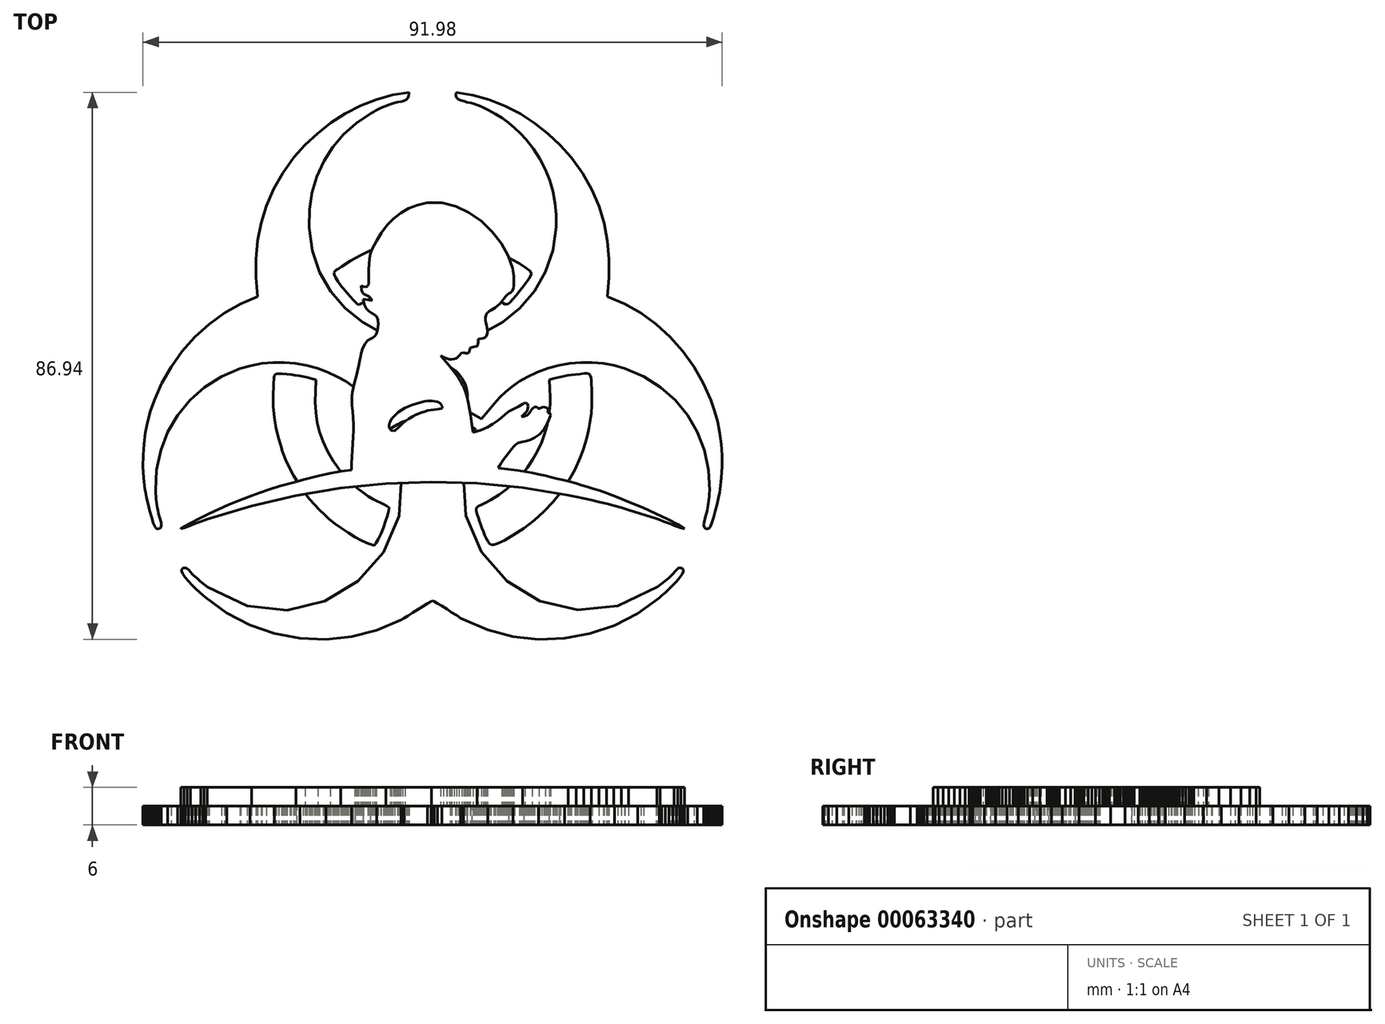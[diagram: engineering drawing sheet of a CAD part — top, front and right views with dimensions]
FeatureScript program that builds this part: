
annotation { "Feature Type Name" : "Feature", "Feature Type Description" : "" }
export const myFeature = defineFeature(function(context is Context, id is Id, definition is map)
    precondition{}
    {
        {
            var Q0;
            Q0=qCreatedBy(makeId("Top.planeOp"),FACE);
            var sketch = newSketch(context, id + "F0", { "sketchPlane" : qUnion([Q0])});
            skLineSegment(sketch, "E0", {"start": v(-39.96, -25.84) * mm, "end": v(-40, -25.92) * mm});
            skLineSegment(sketch, "E1", {"start": v(-40, -25.92) * mm, "end": v(-39.49, -25.75) * mm});
            skLineSegment(sketch, "E2", {"start": v(-39.49, -25.75) * mm, "end": v(-38.96, -25.56) * mm});
            skLineSegment(sketch, "E3", {"start": v(-38.96, -25.56) * mm, "end": v(-38.44, -25.37) * mm});
            skLineSegment(sketch, "E4", {"start": v(-38.44, -25.37) * mm, "end": v(-37.9, -25.16) * mm});
            skLineSegment(sketch, "E5", {"start": v(-37.9, -25.16) * mm, "end": v(-37.38, -24.95) * mm});
            skLineSegment(sketch, "E6", {"start": v(-37.38, -24.95) * mm, "end": v(-36.84, -24.75) * mm});
            skLineSegment(sketch, "E7", {"start": v(-36.84, -24.75) * mm, "end": v(-36.3, -24.55) * mm});
            skLineSegment(sketch, "E8", {"start": v(-36.3, -24.55) * mm, "end": v(-35.77, -24.36) * mm});
            skLineSegment(sketch, "E9", {"start": v(-35.77, -24.36) * mm, "end": v(-28.76, -22.26) * mm});
            skLineSegment(sketch, "E10", {"start": v(-28.76, -22.26) * mm, "end": v(-21.7, -20.62) * mm});
            skLineSegment(sketch, "E11", {"start": v(-21.7, -20.62) * mm, "end": v(-14.56, -19.44) * mm});
            skLineSegment(sketch, "E12", {"start": v(-14.56, -19.44) * mm, "end": v(-7.4, -18.72) * mm});
            skLineSegment(sketch, "E13", {"start": v(-7.4, -18.72) * mm, "end": v(-0.18, -18.47) * mm});
            skLineSegment(sketch, "E14", {"start": v(-0.18, -18.47) * mm, "end": v(7.05, -18.68) * mm});
            skLineSegment(sketch, "E15", {"start": v(7.05, -18.68) * mm, "end": v(14.3, -19.38) * mm});
            skLineSegment(sketch, "E16", {"start": v(14.3, -19.38) * mm, "end": v(21.57, -20.55) * mm});
            skLineSegment(sketch, "E17", {"start": v(21.57, -20.55) * mm, "end": v(22.8, -20.8) * mm});
            skLineSegment(sketch, "E18", {"start": v(22.8, -20.8) * mm, "end": v(24.01, -21.05) * mm});
            skLineSegment(sketch, "E19", {"start": v(24.01, -21.05) * mm, "end": v(25.22, -21.32) * mm});
            skLineSegment(sketch, "E20", {"start": v(25.22, -21.32) * mm, "end": v(26.42, -21.6) * mm});
            skLineSegment(sketch, "E21", {"start": v(26.42, -21.6) * mm, "end": v(27.61, -21.9) * mm});
            skLineSegment(sketch, "E22", {"start": v(27.61, -21.9) * mm, "end": v(28.8, -22.21) * mm});
            skLineSegment(sketch, "E23", {"start": v(28.8, -22.21) * mm, "end": v(29.97, -22.54) * mm});
            skLineSegment(sketch, "E24", {"start": v(29.97, -22.54) * mm, "end": v(31.13, -22.88) * mm});
            skLineSegment(sketch, "E25", {"start": v(31.13, -22.88) * mm, "end": v(35.63, -24.33) * mm});
            skLineSegment(sketch, "E26", {"start": v(35.63, -24.33) * mm, "end": v(36.17, -24.52) * mm});
            skLineSegment(sketch, "E27", {"start": v(36.17, -24.52) * mm, "end": v(36.73, -24.73) * mm});
            skLineSegment(sketch, "E28", {"start": v(36.73, -24.73) * mm, "end": v(37.28, -24.95) * mm});
            skLineSegment(sketch, "E29", {"start": v(37.28, -24.95) * mm, "end": v(37.84, -25.16) * mm});
            skLineSegment(sketch, "E30", {"start": v(37.84, -25.16) * mm, "end": v(38.39, -25.37) * mm});
            skLineSegment(sketch, "E31", {"start": v(38.39, -25.37) * mm, "end": v(38.94, -25.57) * mm});
            skLineSegment(sketch, "E32", {"start": v(38.94, -25.57) * mm, "end": v(39.47, -25.76) * mm});
            skLineSegment(sketch, "E33", {"start": v(39.47, -25.76) * mm, "end": v(40, -25.92) * mm});
            skLineSegment(sketch, "E34", {"start": v(40, -25.92) * mm, "end": v(38.93, -25.2) * mm});
            skLineSegment(sketch, "E35", {"start": v(38.93, -25.2) * mm, "end": v(37.37, -24.37) * mm});
            skLineSegment(sketch, "E36", {"start": v(37.37, -24.37) * mm, "end": v(35.47, -23.47) * mm});
            skLineSegment(sketch, "E37", {"start": v(35.47, -23.47) * mm, "end": v(33.4, -22.55) * mm});
            skLineSegment(sketch, "E38", {"start": v(33.4, -22.55) * mm, "end": v(31.32, -21.67) * mm});
            skLineSegment(sketch, "E39", {"start": v(31.32, -21.67) * mm, "end": v(29.36, -20.9) * mm});
            skLineSegment(sketch, "E40", {"start": v(29.36, -20.9) * mm, "end": v(27.7, -20.25) * mm});
            skLineSegment(sketch, "E41", {"start": v(27.7, -20.25) * mm, "end": v(26.47, -19.82) * mm});
            skLineSegment(sketch, "E42", {"start": v(26.47, -19.82) * mm, "end": v(25.54, -19.52) * mm});
            skLineSegment(sketch, "E43", {"start": v(25.54, -19.52) * mm, "end": v(24.6, -19.22) * mm});
            skLineSegment(sketch, "E44", {"start": v(24.6, -19.22) * mm, "end": v(23.67, -18.95) * mm});
            skLineSegment(sketch, "E45", {"start": v(23.67, -18.95) * mm, "end": v(22.72, -18.68) * mm});
            skLineSegment(sketch, "E46", {"start": v(22.72, -18.68) * mm, "end": v(21.77, -18.42) * mm});
            skLineSegment(sketch, "E47", {"start": v(21.77, -18.42) * mm, "end": v(20.8, -18.17) * mm});
            skLineSegment(sketch, "E48", {"start": v(20.8, -18.17) * mm, "end": v(19.84, -17.93) * mm});
            skLineSegment(sketch, "E49", {"start": v(19.84, -17.93) * mm, "end": v(18.85, -17.7) * mm});
            skLineSegment(sketch, "E50", {"start": v(18.85, -17.7) * mm, "end": v(17.91, -17.48) * mm});
            skLineSegment(sketch, "E51", {"start": v(17.91, -17.48) * mm, "end": v(16.89, -17.26) * mm});
            skLineSegment(sketch, "E52", {"start": v(16.89, -17.26) * mm, "end": v(15.8, -17.03) * mm});
            skLineSegment(sketch, "E53", {"start": v(15.8, -17.03) * mm, "end": v(14.69, -16.82) * mm});
            skLineSegment(sketch, "E54", {"start": v(14.69, -16.82) * mm, "end": v(13.57, -16.63) * mm});
            skLineSegment(sketch, "E55", {"start": v(13.57, -16.63) * mm, "end": v(12.47, -16.47) * mm});
            skLineSegment(sketch, "E56", {"start": v(12.47, -16.47) * mm, "end": v(11.43, -16.34) * mm});
            skLineSegment(sketch, "E57", {"start": v(11.43, -16.34) * mm, "end": v(10.45, -16.25) * mm});
            skLineSegment(sketch, "E58", {"start": v(10.45, -16.25) * mm, "end": v(10.62, -15.92) * mm});
            skLineSegment(sketch, "E59", {"start": v(10.62, -15.92) * mm, "end": v(10.9, -15.47) * mm});
            skLineSegment(sketch, "E60", {"start": v(10.9, -15.47) * mm, "end": v(11.27, -14.93) * mm});
            skLineSegment(sketch, "E61", {"start": v(11.27, -14.93) * mm, "end": v(11.69, -14.36) * mm});
            skLineSegment(sketch, "E62", {"start": v(11.69, -14.36) * mm, "end": v(12.12, -13.8) * mm});
            skLineSegment(sketch, "E63", {"start": v(12.12, -13.8) * mm, "end": v(12.54, -13.27) * mm});
            skLineSegment(sketch, "E64", {"start": v(12.54, -13.27) * mm, "end": v(12.91, -12.82) * mm});
            skLineSegment(sketch, "E65", {"start": v(12.91, -12.82) * mm, "end": v(13.2, -12.5) * mm});
            skLineSegment(sketch, "E66", {"start": v(13.2, -12.5) * mm, "end": v(13.6, -12.26) * mm});
            skLineSegment(sketch, "E67", {"start": v(13.6, -12.26) * mm, "end": v(14.12, -12.1) * mm});
            skLineSegment(sketch, "E68", {"start": v(14.12, -12.1) * mm, "end": v(14.76, -11.96) * mm});
            skLineSegment(sketch, "E69", {"start": v(14.76, -11.96) * mm, "end": v(15.47, -11.76) * mm});
            skLineSegment(sketch, "E70", {"start": v(15.47, -11.76) * mm, "end": v(16.2, -11.44) * mm});
            skLineSegment(sketch, "E71", {"start": v(16.2, -11.44) * mm, "end": v(16.95, -10.92) * mm});
            skLineSegment(sketch, "E72", {"start": v(16.95, -10.92) * mm, "end": v(17.65, -10.14) * mm});
            skLineSegment(sketch, "E73", {"start": v(17.65, -10.14) * mm, "end": v(18.28, -9.02) * mm});
            skLineSegment(sketch, "E74", {"start": v(18.28, -9.02) * mm, "end": v(18.72, -7.84) * mm});
            skLineSegment(sketch, "E75", {"start": v(18.72, -7.84) * mm, "end": v(18.7, -7.63) * mm});
            skLineSegment(sketch, "E76", {"start": v(18.7, -7.63) * mm, "end": v(18.66, -7.56) * mm});
            skLineSegment(sketch, "E77", {"start": v(18.66, -7.56) * mm, "end": v(18.61, -7.56) * mm});
            skLineSegment(sketch, "E78", {"start": v(18.61, -7.56) * mm, "end": v(18.55, -7.53) * mm});
            skLineSegment(sketch, "E79", {"start": v(18.55, -7.53) * mm, "end": v(18.33, -7.4) * mm});
            skLineSegment(sketch, "E80", {"start": v(18.33, -7.4) * mm, "end": v(18.32, -7.3) * mm});
            skLineSegment(sketch, "E81", {"start": v(18.32, -7.3) * mm, "end": v(18.32, -7.25) * mm});
            skLineSegment(sketch, "E82", {"start": v(18.32, -7.25) * mm, "end": v(18.35, -7.24) * mm});
            skLineSegment(sketch, "E83", {"start": v(18.35, -7.24) * mm, "end": v(18.44, -7.24) * mm});
            skLineSegment(sketch, "E84", {"start": v(18.44, -7.24) * mm, "end": v(18.4, -7.02) * mm});
            skLineSegment(sketch, "E85", {"start": v(18.4, -7.02) * mm, "end": v(18.28, -6.83) * mm});
            skLineSegment(sketch, "E86", {"start": v(18.28, -6.83) * mm, "end": v(18.1, -6.68) * mm});
            skLineSegment(sketch, "E87", {"start": v(18.1, -6.68) * mm, "end": v(17.9, -6.59) * mm});
            skLineSegment(sketch, "E88", {"start": v(17.9, -6.59) * mm, "end": v(17.65, -6.55) * mm});
            skLineSegment(sketch, "E89", {"start": v(17.65, -6.55) * mm, "end": v(17.4, -6.58) * mm});
            skLineSegment(sketch, "E90", {"start": v(17.4, -6.58) * mm, "end": v(17.12, -6.69) * mm});
            skLineSegment(sketch, "E91", {"start": v(17.12, -6.69) * mm, "end": v(16.86, -6.87) * mm});
            skLineSegment(sketch, "E92", {"start": v(16.86, -6.87) * mm, "end": v(16.7, -6.63) * mm});
            skLineSegment(sketch, "E93", {"start": v(16.7, -6.63) * mm, "end": v(16.51, -6.52) * mm});
            skLineSegment(sketch, "E94", {"start": v(16.51, -6.52) * mm, "end": v(16.33, -6.52) * mm});
            skLineSegment(sketch, "E95", {"start": v(16.33, -6.52) * mm, "end": v(16.14, -6.6) * mm});
            skLineSegment(sketch, "E96", {"start": v(16.14, -6.6) * mm, "end": v(15.96, -6.74) * mm});
            skLineSegment(sketch, "E97", {"start": v(15.96, -6.74) * mm, "end": v(15.8, -6.9) * mm});
            skLineSegment(sketch, "E98", {"start": v(15.8, -6.9) * mm, "end": v(15.66, -7.08) * mm});
            skLineSegment(sketch, "E99", {"start": v(15.66, -7.08) * mm, "end": v(15.55, -7.23) * mm});
            skLineSegment(sketch, "E100", {"start": v(15.55, -7.23) * mm, "end": v(15.43, -7.39) * mm});
            skLineSegment(sketch, "E101", {"start": v(15.43, -7.39) * mm, "end": v(15.3, -7.55) * mm});
            skLineSegment(sketch, "E102", {"start": v(15.3, -7.55) * mm, "end": v(15.17, -7.7) * mm});
            skLineSegment(sketch, "E103", {"start": v(15.17, -7.7) * mm, "end": v(15.02, -7.84) * mm});
            skLineSegment(sketch, "E104", {"start": v(15.02, -7.84) * mm, "end": v(14.84, -7.95) * mm});
            skLineSegment(sketch, "E105", {"start": v(14.84, -7.95) * mm, "end": v(14.63, -8.03) * mm});
            skLineSegment(sketch, "E106", {"start": v(14.63, -8.03) * mm, "end": v(14.38, -8.08) * mm});
            skLineSegment(sketch, "E107", {"start": v(14.38, -8.08) * mm, "end": v(14.09, -8.07) * mm});
            skLineSegment(sketch, "E108", {"start": v(14.09, -8.07) * mm, "end": v(14.28, -7.91) * mm});
            skLineSegment(sketch, "E109", {"start": v(14.28, -7.91) * mm, "end": v(14.5, -7.73) * mm});
            skLineSegment(sketch, "E110", {"start": v(14.5, -7.73) * mm, "end": v(14.72, -7.53) * mm});
            skLineSegment(sketch, "E111", {"start": v(14.72, -7.53) * mm, "end": v(14.92, -7.29) * mm});
            skLineSegment(sketch, "E112", {"start": v(14.92, -7.29) * mm, "end": v(15.08, -7.02) * mm});
            skLineSegment(sketch, "E113", {"start": v(15.08, -7.02) * mm, "end": v(15.17, -6.73) * mm});
            skLineSegment(sketch, "E114", {"start": v(15.17, -6.73) * mm, "end": v(15.17, -6.4) * mm});
            skLineSegment(sketch, "E115", {"start": v(15.17, -6.4) * mm, "end": v(15.05, -6.04) * mm});
            skLineSegment(sketch, "E116", {"start": v(15.05, -6.04) * mm, "end": v(14.9, -5.93) * mm});
            skLineSegment(sketch, "E117", {"start": v(14.9, -5.93) * mm, "end": v(14.72, -5.9) * mm});
            skLineSegment(sketch, "E118", {"start": v(14.72, -5.9) * mm, "end": v(14.52, -5.96) * mm});
            skLineSegment(sketch, "E119", {"start": v(14.52, -5.96) * mm, "end": v(14.28, -6.08) * mm});
            skLineSegment(sketch, "E120", {"start": v(14.28, -6.08) * mm, "end": v(13.7, -6.44) * mm});
            skLineSegment(sketch, "E121", {"start": v(13.7, -6.44) * mm, "end": v(12.91, -6.86) * mm});
            skLineSegment(sketch, "E122", {"start": v(12.91, -6.86) * mm, "end": v(12.18, -7.25) * mm});
            skLineSegment(sketch, "E123", {"start": v(12.18, -7.25) * mm, "end": v(11.53, -7.72) * mm});
            skLineSegment(sketch, "E124", {"start": v(11.53, -7.72) * mm, "end": v(10.92, -8.22) * mm});
            skLineSegment(sketch, "E125", {"start": v(10.92, -8.22) * mm, "end": v(10.28, -8.74) * mm});
            skLineSegment(sketch, "E126", {"start": v(10.28, -8.74) * mm, "end": v(9.57, -9.26) * mm});
            skLineSegment(sketch, "E127", {"start": v(9.57, -9.26) * mm, "end": v(8.72, -9.76) * mm});
            skLineSegment(sketch, "E128", {"start": v(8.72, -9.76) * mm, "end": v(7.7, -10.2) * mm});
            skLineSegment(sketch, "E129", {"start": v(7.7, -10.2) * mm, "end": v(6.43, -10.6) * mm});
            skLineSegment(sketch, "E130", {"start": v(6.43, -10.6) * mm, "end": v(6.32, -9.78) * mm});
            skLineSegment(sketch, "E131", {"start": v(6.32, -9.78) * mm, "end": v(6.19, -8.85) * mm});
            skLineSegment(sketch, "E132", {"start": v(6.19, -8.85) * mm, "end": v(6.03, -7.86) * mm});
            skLineSegment(sketch, "E133", {"start": v(6.03, -7.86) * mm, "end": v(5.86, -6.84) * mm});
            skLineSegment(sketch, "E134", {"start": v(5.86, -6.84) * mm, "end": v(5.67, -5.84) * mm});
            skLineSegment(sketch, "E135", {"start": v(5.67, -5.84) * mm, "end": v(5.46, -4.91) * mm});
            skLineSegment(sketch, "E136", {"start": v(5.46, -4.91) * mm, "end": v(5.22, -4.09) * mm});
            skLineSegment(sketch, "E137", {"start": v(5.22, -4.09) * mm, "end": v(4.97, -3.41) * mm});
            skLineSegment(sketch, "E138", {"start": v(4.97, -3.41) * mm, "end": v(4.79, -3.05) * mm});
            skLineSegment(sketch, "E139", {"start": v(4.79, -3.05) * mm, "end": v(4.59, -2.69) * mm});
            skLineSegment(sketch, "E140", {"start": v(4.59, -2.69) * mm, "end": v(4.37, -2.33) * mm});
            skLineSegment(sketch, "E141", {"start": v(4.37, -2.33) * mm, "end": v(4.14, -1.98) * mm});
            skLineSegment(sketch, "E142", {"start": v(4.14, -1.98) * mm, "end": v(3.67, -1.32) * mm});
            skLineSegment(sketch, "E143", {"start": v(3.67, -1.32) * mm, "end": v(3.24, -0.74) * mm});
            skLineSegment(sketch, "E144", {"start": v(3.24, -0.74) * mm, "end": v(2.78, -0.16) * mm});
            skLineSegment(sketch, "E145", {"start": v(2.78, -0.16) * mm, "end": v(2.26, 0.5) * mm});
            skLineSegment(sketch, "E146", {"start": v(2.26, 0.5) * mm, "end": v(1.73, 1.11) * mm});
            skLineSegment(sketch, "E147", {"start": v(1.73, 1.11) * mm, "end": v(1.27, 1.6) * mm});
            skLineSegment(sketch, "E148", {"start": v(1.27, 1.6) * mm, "end": v(1.82, 1.37) * mm});
            skLineSegment(sketch, "E149", {"start": v(1.82, 1.37) * mm, "end": v(2.3, 1.19) * mm});
            skLineSegment(sketch, "E150", {"start": v(2.3, 1.19) * mm, "end": v(2.71, 1.06) * mm});
            skLineSegment(sketch, "E151", {"start": v(2.71, 1.06) * mm, "end": v(3.1, 1.01) * mm});
            skLineSegment(sketch, "E152", {"start": v(3.1, 1.01) * mm, "end": v(3.47, 1.07) * mm});
            skLineSegment(sketch, "E153", {"start": v(3.47, 1.07) * mm, "end": v(3.83, 1.25) * mm});
            skLineSegment(sketch, "E154", {"start": v(3.83, 1.25) * mm, "end": v(4.22, 1.58) * mm});
            skLineSegment(sketch, "E155", {"start": v(4.22, 1.58) * mm, "end": v(4.64, 2.1) * mm});
            skLineSegment(sketch, "E156", {"start": v(4.64, 2.1) * mm, "end": v(4.96, 2.05) * mm});
            skLineSegment(sketch, "E157", {"start": v(4.96, 2.05) * mm, "end": v(5.22, 2.02) * mm});
            skLineSegment(sketch, "E158", {"start": v(5.22, 2.02) * mm, "end": v(5.34, 2) * mm});
            skLineSegment(sketch, "E159", {"start": v(5.34, 2) * mm, "end": v(5.47, 2.01) * mm});
            skLineSegment(sketch, "E160", {"start": v(5.47, 2.01) * mm, "end": v(5.61, 2.03) * mm});
            skLineSegment(sketch, "E161", {"start": v(5.61, 2.03) * mm, "end": v(5.78, 2.08) * mm});
            skLineSegment(sketch, "E162", {"start": v(5.78, 2.08) * mm, "end": v(6.01, 2.9) * mm});
            skLineSegment(sketch, "E163", {"start": v(6.01, 2.9) * mm, "end": v(6.72, 3.04) * mm});
            skLineSegment(sketch, "E164", {"start": v(6.72, 3.04) * mm, "end": v(7.06, 3.11) * mm});
            skLineSegment(sketch, "E165", {"start": v(7.06, 3.11) * mm, "end": v(7.14, 3.21) * mm});
            skLineSegment(sketch, "E166", {"start": v(7.14, 3.21) * mm, "end": v(7.19, 3.41) * mm});
            skLineSegment(sketch, "E167", {"start": v(7.19, 3.41) * mm, "end": v(7.23, 3.75) * mm});
            skLineSegment(sketch, "E168", {"start": v(7.23, 3.75) * mm, "end": v(7.3, 4.26) * mm});
            skLineSegment(sketch, "E169", {"start": v(7.3, 4.26) * mm, "end": v(7.74, 4.33) * mm});
            skLineSegment(sketch, "E170", {"start": v(7.74, 4.33) * mm, "end": v(8.1, 4.42) * mm});
            skLineSegment(sketch, "E171", {"start": v(8.1, 4.42) * mm, "end": v(8.25, 4.48) * mm});
            skLineSegment(sketch, "E172", {"start": v(8.25, 4.48) * mm, "end": v(8.4, 4.56) * mm});
            skLineSegment(sketch, "E173", {"start": v(8.4, 4.56) * mm, "end": v(8.51, 4.67) * mm});
            skLineSegment(sketch, "E174", {"start": v(8.51, 4.67) * mm, "end": v(8.62, 4.82) * mm});
            skLineSegment(sketch, "E175", {"start": v(8.62, 4.82) * mm, "end": v(8.74, 5.22) * mm});
            skLineSegment(sketch, "E176", {"start": v(8.74, 5.22) * mm, "end": v(8.75, 5.62) * mm});
            skLineSegment(sketch, "E177", {"start": v(8.75, 5.62) * mm, "end": v(8.67, 6.04) * mm});
            skLineSegment(sketch, "E178", {"start": v(8.67, 6.04) * mm, "end": v(8.56, 6.46) * mm});
            skLineSegment(sketch, "E179", {"start": v(8.56, 6.46) * mm, "end": v(8.45, 6.88) * mm});
            skLineSegment(sketch, "E180", {"start": v(8.45, 6.88) * mm, "end": v(8.38, 7.3) * mm});
            skLineSegment(sketch, "E181", {"start": v(8.38, 7.3) * mm, "end": v(8.38, 7.71) * mm});
            skLineSegment(sketch, "E182", {"start": v(8.38, 7.71) * mm, "end": v(8.51, 8.12) * mm});
            skLineSegment(sketch, "E183", {"start": v(8.51, 8.12) * mm, "end": v(8.67, 8.37) * mm});
            skLineSegment(sketch, "E184", {"start": v(8.67, 8.37) * mm, "end": v(8.85, 8.55) * mm});
            skLineSegment(sketch, "E185", {"start": v(8.85, 8.55) * mm, "end": v(9.07, 8.7) * mm});
            skLineSegment(sketch, "E186", {"start": v(9.07, 8.7) * mm, "end": v(9.32, 8.85) * mm});
            skLineSegment(sketch, "E187", {"start": v(9.32, 8.85) * mm, "end": v(9.6, 9.02) * mm});
            skLineSegment(sketch, "E188", {"start": v(9.6, 9.02) * mm, "end": v(9.94, 9.24) * mm});
            skLineSegment(sketch, "E189", {"start": v(9.94, 9.24) * mm, "end": v(10.31, 9.54) * mm});
            skLineSegment(sketch, "E190", {"start": v(10.31, 9.54) * mm, "end": v(10.73, 9.94) * mm});
            skLineSegment(sketch, "E191", {"start": v(10.73, 9.94) * mm, "end": v(11, 10.24) * mm});
            skLineSegment(sketch, "E192", {"start": v(11, 10.24) * mm, "end": v(11.2, 10.5) * mm});
            skLineSegment(sketch, "E193", {"start": v(11.2, 10.5) * mm, "end": v(11.4, 10.77) * mm});
            skLineSegment(sketch, "E194", {"start": v(11.4, 10.77) * mm, "end": v(11.62, 11.07) * mm});
            skLineSegment(sketch, "E195", {"start": v(11.62, 11.07) * mm, "end": v(11.8, 11.27) * mm});
            skLineSegment(sketch, "E196", {"start": v(11.8, 11.27) * mm, "end": v(11.97, 11.41) * mm});
            skLineSegment(sketch, "E197", {"start": v(11.97, 11.41) * mm, "end": v(12.13, 11.51) * mm});
            skLineSegment(sketch, "E198", {"start": v(12.13, 11.51) * mm, "end": v(12.28, 11.59) * mm});
            skLineSegment(sketch, "E199", {"start": v(12.28, 11.59) * mm, "end": v(12.41, 11.66) * mm});
            skLineSegment(sketch, "E200", {"start": v(12.41, 11.66) * mm, "end": v(12.54, 11.74) * mm});
            skLineSegment(sketch, "E201", {"start": v(12.54, 11.74) * mm, "end": v(12.65, 11.84) * mm});
            skLineSegment(sketch, "E202", {"start": v(12.65, 11.84) * mm, "end": v(12.74, 11.99) * mm});
            skLineSegment(sketch, "E203", {"start": v(12.74, 11.99) * mm, "end": v(12.85, 12.31) * mm});
            skLineSegment(sketch, "E204", {"start": v(12.85, 12.31) * mm, "end": v(12.9, 12.73) * mm});
            skLineSegment(sketch, "E205", {"start": v(12.9, 12.73) * mm, "end": v(12.93, 13.2) * mm});
            skLineSegment(sketch, "E206", {"start": v(12.93, 13.2) * mm, "end": v(12.92, 13.71) * mm});
            skLineSegment(sketch, "E207", {"start": v(12.92, 13.71) * mm, "end": v(12.89, 14.22) * mm});
            skLineSegment(sketch, "E208", {"start": v(12.89, 14.22) * mm, "end": v(12.84, 14.7) * mm});
            skLineSegment(sketch, "E209", {"start": v(12.84, 14.7) * mm, "end": v(12.77, 15.14) * mm});
            skLineSegment(sketch, "E210", {"start": v(12.77, 15.14) * mm, "end": v(12.7, 15.49) * mm});
            skLineSegment(sketch, "E211", {"start": v(12.7, 15.49) * mm, "end": v(12.02, 17.47) * mm});
            skLineSegment(sketch, "E212", {"start": v(12.02, 17.47) * mm, "end": v(10.94, 19.44) * mm});
            skLineSegment(sketch, "E213", {"start": v(10.94, 19.44) * mm, "end": v(9.5, 21.3) * mm});
            skLineSegment(sketch, "E214", {"start": v(9.5, 21.3) * mm, "end": v(7.78, 22.98) * mm});
            skLineSegment(sketch, "E215", {"start": v(7.78, 22.98) * mm, "end": v(5.83, 24.37) * mm});
            skLineSegment(sketch, "E216", {"start": v(5.83, 24.37) * mm, "end": v(3.7, 25.38) * mm});
            skLineSegment(sketch, "E217", {"start": v(3.7, 25.38) * mm, "end": v(1.46, 25.92) * mm});
            skLineSegment(sketch, "E218", {"start": v(1.46, 25.92) * mm, "end": v(-0.84, 25.91) * mm});
            skLineSegment(sketch, "E219", {"start": v(-0.84, 25.91) * mm, "end": v(-2.4, 25.57) * mm});
            skLineSegment(sketch, "E220", {"start": v(-2.4, 25.57) * mm, "end": v(-3.8, 25.03) * mm});
            skLineSegment(sketch, "E221", {"start": v(-3.8, 25.03) * mm, "end": v(-5.05, 24.3) * mm});
            skLineSegment(sketch, "E222", {"start": v(-5.05, 24.3) * mm, "end": v(-6.18, 23.4) * mm});
            skLineSegment(sketch, "E223", {"start": v(-6.18, 23.4) * mm, "end": v(-7.2, 22.36) * mm});
            skLineSegment(sketch, "E224", {"start": v(-7.2, 22.36) * mm, "end": v(-8.1, 21.19) * mm});
            skLineSegment(sketch, "E225", {"start": v(-8.1, 21.19) * mm, "end": v(-8.9, 19.9) * mm});
            skLineSegment(sketch, "E226", {"start": v(-8.9, 19.9) * mm, "end": v(-9.6, 18.52) * mm});
            skLineSegment(sketch, "E227", {"start": v(-9.6, 18.52) * mm, "end": v(-9.86, 17.79) * mm});
            skLineSegment(sketch, "E228", {"start": v(-9.86, 17.79) * mm, "end": v(-10.02, 17) * mm});
            skLineSegment(sketch, "E229", {"start": v(-10.02, 17) * mm, "end": v(-10.1, 16.16) * mm});
            skLineSegment(sketch, "E230", {"start": v(-10.1, 16.16) * mm, "end": v(-10.13, 15.35) * mm});
            skLineSegment(sketch, "E231", {"start": v(-10.13, 15.35) * mm, "end": v(-10.13, 14.58) * mm});
            skLineSegment(sketch, "E232", {"start": v(-10.13, 14.58) * mm, "end": v(-10.11, 13.9) * mm});
            skLineSegment(sketch, "E233", {"start": v(-10.11, 13.9) * mm, "end": v(-10.12, 13.36) * mm});
            skLineSegment(sketch, "E234", {"start": v(-10.12, 13.36) * mm, "end": v(-10.16, 12.98) * mm});
            skLineSegment(sketch, "E235", {"start": v(-10.16, 12.98) * mm, "end": v(-10.24, 12.77) * mm});
            skLineSegment(sketch, "E236", {"start": v(-10.24, 12.77) * mm, "end": v(-10.34, 12.64) * mm});
            skLineSegment(sketch, "E237", {"start": v(-10.34, 12.64) * mm, "end": v(-10.47, 12.56) * mm});
            skLineSegment(sketch, "E238", {"start": v(-10.47, 12.56) * mm, "end": v(-10.62, 12.54) * mm});
            skLineSegment(sketch, "E239", {"start": v(-10.62, 12.54) * mm, "end": v(-10.97, 12.6) * mm});
            skLineSegment(sketch, "E240", {"start": v(-10.97, 12.6) * mm, "end": v(-11.36, 12.7) * mm});
            skLineSegment(sketch, "E241", {"start": v(-11.36, 12.7) * mm, "end": v(-11.29, 12.1) * mm});
            skLineSegment(sketch, "E242", {"start": v(-11.29, 12.1) * mm, "end": v(-11.16, 11.71) * mm});
            skLineSegment(sketch, "E243", {"start": v(-11.16, 11.71) * mm, "end": v(-10.96, 11.47) * mm});
            skLineSegment(sketch, "E244", {"start": v(-10.96, 11.47) * mm, "end": v(-10.73, 11.32) * mm});
            skLineSegment(sketch, "E245", {"start": v(-10.73, 11.32) * mm, "end": v(-10.46, 11.2) * mm});
            skLineSegment(sketch, "E246", {"start": v(-10.46, 11.2) * mm, "end": v(-10.16, 11.05) * mm});
            skLineSegment(sketch, "E247", {"start": v(-10.16, 11.05) * mm, "end": v(-9.86, 10.8) * mm});
            skLineSegment(sketch, "E248", {"start": v(-9.86, 10.8) * mm, "end": v(-9.55, 10.4) * mm});
            skLineSegment(sketch, "E249", {"start": v(-9.55, 10.4) * mm, "end": v(-11.06, 10.65) * mm});
            skLineSegment(sketch, "E250", {"start": v(-11.06, 10.65) * mm, "end": v(-10.87, 9.73) * mm});
            skLineSegment(sketch, "E251", {"start": v(-10.87, 9.73) * mm, "end": v(-10.54, 9.1) * mm});
            skLineSegment(sketch, "E252", {"start": v(-10.54, 9.1) * mm, "end": v(-10.12, 8.7) * mm});
            skLineSegment(sketch, "E253", {"start": v(-10.12, 8.7) * mm, "end": v(-9.68, 8.4) * mm});
            skLineSegment(sketch, "E254", {"start": v(-9.68, 8.4) * mm, "end": v(-9.25, 8.12) * mm});
            skLineSegment(sketch, "E255", {"start": v(-9.25, 8.12) * mm, "end": v(-8.9, 7.8) * mm});
            skLineSegment(sketch, "E256", {"start": v(-8.9, 7.8) * mm, "end": v(-8.67, 7.32) * mm});
            skLineSegment(sketch, "E257", {"start": v(-8.67, 7.32) * mm, "end": v(-8.6, 6.62) * mm});
            skLineSegment(sketch, "E258", {"start": v(-8.6, 6.62) * mm, "end": v(-8.72, 5.64) * mm});
            skLineSegment(sketch, "E259", {"start": v(-8.72, 5.64) * mm, "end": v(-8.92, 5.04) * mm});
            skLineSegment(sketch, "E260", {"start": v(-8.92, 5.04) * mm, "end": v(-9.2, 4.69) * mm});
            skLineSegment(sketch, "E261", {"start": v(-9.2, 4.69) * mm, "end": v(-9.53, 4.48) * mm});
            skLineSegment(sketch, "E262", {"start": v(-9.53, 4.48) * mm, "end": v(-9.91, 4.3) * mm});
            skLineSegment(sketch, "E263", {"start": v(-9.91, 4.3) * mm, "end": v(-10.32, 4.01) * mm});
            skLineSegment(sketch, "E264", {"start": v(-10.32, 4.01) * mm, "end": v(-10.73, 3.52) * mm});
            skLineSegment(sketch, "E265", {"start": v(-10.73, 3.52) * mm, "end": v(-11.14, 2.7) * mm});
            skLineSegment(sketch, "E266", {"start": v(-11.14, 2.7) * mm, "end": v(-11.25, 2.37) * mm});
            skLineSegment(sketch, "E267", {"start": v(-11.25, 2.37) * mm, "end": v(-11.34, 1.97) * mm});
            skLineSegment(sketch, "E268", {"start": v(-11.34, 1.97) * mm, "end": v(-11.43, 1.52) * mm});
            skLineSegment(sketch, "E269", {"start": v(-11.43, 1.52) * mm, "end": v(-11.52, 1.03) * mm});
            skLineSegment(sketch, "E270", {"start": v(-11.52, 1.03) * mm, "end": v(-11.7, 0.04) * mm});
            skLineSegment(sketch, "E271", {"start": v(-11.7, 0.04) * mm, "end": v(-11.9, -0.83) * mm});
            skLineSegment(sketch, "E272", {"start": v(-11.9, -0.83) * mm, "end": v(-12.13, -1.66) * mm});
            skLineSegment(sketch, "E273", {"start": v(-12.13, -1.66) * mm, "end": v(-12.37, -2.5) * mm});
            skLineSegment(sketch, "E274", {"start": v(-12.37, -2.5) * mm, "end": v(-12.58, -3.37) * mm});
            skLineSegment(sketch, "E275", {"start": v(-12.58, -3.37) * mm, "end": v(-12.74, -4.26) * mm});
            skLineSegment(sketch, "E276", {"start": v(-12.74, -4.26) * mm, "end": v(-12.8, -4.84) * mm});
            skLineSegment(sketch, "E277", {"start": v(-12.8, -4.84) * mm, "end": v(-12.83, -5.36) * mm});
            skLineSegment(sketch, "E278", {"start": v(-12.83, -5.36) * mm, "end": v(-12.82, -5.84) * mm});
            skLineSegment(sketch, "E279", {"start": v(-12.82, -5.84) * mm, "end": v(-12.79, -6.3) * mm});
            skLineSegment(sketch, "E280", {"start": v(-12.79, -6.3) * mm, "end": v(-12.69, -7.2) * mm});
            skLineSegment(sketch, "E281", {"start": v(-12.69, -7.2) * mm, "end": v(-12.6, -8.24) * mm});
            skLineSegment(sketch, "E282", {"start": v(-12.6, -8.24) * mm, "end": v(-12.56, -9.24) * mm});
            skLineSegment(sketch, "E283", {"start": v(-12.56, -9.24) * mm, "end": v(-12.57, -10.27) * mm});
            skLineSegment(sketch, "E284", {"start": v(-12.57, -10.27) * mm, "end": v(-12.62, -11.32) * mm});
            skLineSegment(sketch, "E285", {"start": v(-12.62, -11.32) * mm, "end": v(-12.68, -12.37) * mm});
            skLineSegment(sketch, "E286", {"start": v(-12.68, -12.37) * mm, "end": v(-12.75, -13.43) * mm});
            skLineSegment(sketch, "E287", {"start": v(-12.75, -13.43) * mm, "end": v(-12.82, -14.5) * mm});
            skLineSegment(sketch, "E288", {"start": v(-12.82, -14.5) * mm, "end": v(-12.87, -15.55) * mm});
            skLineSegment(sketch, "E289", {"start": v(-12.87, -15.55) * mm, "end": v(-12.9, -16.59) * mm});
            skLineSegment(sketch, "E290", {"start": v(-12.9, -16.59) * mm, "end": v(-14.45, -16.77) * mm});
            skLineSegment(sketch, "E291", {"start": v(-14.45, -16.77) * mm, "end": v(-16.24, -17.1) * mm});
            skLineSegment(sketch, "E292", {"start": v(-16.24, -17.1) * mm, "end": v(-18.2, -17.52) * mm});
            skLineSegment(sketch, "E293", {"start": v(-18.2, -17.52) * mm, "end": v(-20.25, -18.02) * mm});
            skLineSegment(sketch, "E294", {"start": v(-20.25, -18.02) * mm, "end": v(-22.28, -18.56) * mm});
            skLineSegment(sketch, "E295", {"start": v(-22.28, -18.56) * mm, "end": v(-24.23, -19.12) * mm});
            skLineSegment(sketch, "E296", {"start": v(-24.23, -19.12) * mm, "end": v(-26, -19.66) * mm});
            skLineSegment(sketch, "E297", {"start": v(-26, -19.66) * mm, "end": v(-27.5, -20.16) * mm});
            skLineSegment(sketch, "E298", {"start": v(-27.5, -20.16) * mm, "end": v(-29.21, -20.78) * mm});
            skLineSegment(sketch, "E299", {"start": v(-29.21, -20.78) * mm, "end": v(-30.86, -21.42) * mm});
            skLineSegment(sketch, "E300", {"start": v(-30.86, -21.42) * mm, "end": v(-32.44, -22.1) * mm});
            skLineSegment(sketch, "E301", {"start": v(-32.44, -22.1) * mm, "end": v(-33.98, -22.78) * mm});
            skLineSegment(sketch, "E302", {"start": v(-33.98, -22.78) * mm, "end": v(-35.5, -23.5) * mm});
            skLineSegment(sketch, "E303", {"start": v(-35.5, -23.5) * mm, "end": v(-36.98, -24.25) * mm});
            skLineSegment(sketch, "E304", {"start": v(-36.98, -24.25) * mm, "end": v(-38.47, -25.03) * mm});
            skLineSegment(sketch, "E305", {"start": v(-38.47, -25.03) * mm, "end": v(-39.96, -25.84) * mm});
            skLineSegment(sketch, "E306", {"start": v(-1.22, -5.66) * mm, "end": v(-1.92, -5.8) * mm});
            skLineSegment(sketch, "E307", {"start": v(-1.92, -5.8) * mm, "end": v(-2.6, -5.99) * mm});
            skLineSegment(sketch, "E308", {"start": v(-2.6, -5.99) * mm, "end": v(-3.24, -6.2) * mm});
            skLineSegment(sketch, "E309", {"start": v(-3.24, -6.2) * mm, "end": v(-3.85, -6.44) * mm});
            skLineSegment(sketch, "E310", {"start": v(-3.85, -6.44) * mm, "end": v(-4.42, -6.72) * mm});
            skLineSegment(sketch, "E311", {"start": v(-4.42, -6.72) * mm, "end": v(-4.94, -7.02) * mm});
            skLineSegment(sketch, "E312", {"start": v(-4.94, -7.02) * mm, "end": v(-5.42, -7.35) * mm});
            skLineSegment(sketch, "E313", {"start": v(-5.42, -7.35) * mm, "end": v(-5.84, -7.71) * mm});
            skLineSegment(sketch, "E314", {"start": v(-5.84, -7.71) * mm, "end": v(-6.43, -8.36) * mm});
            skLineSegment(sketch, "E315", {"start": v(-6.43, -8.36) * mm, "end": v(-6.78, -8.94) * mm});
            skLineSegment(sketch, "E316", {"start": v(-6.78, -8.94) * mm, "end": v(-6.91, -9.42) * mm});
            skLineSegment(sketch, "E317", {"start": v(-6.91, -9.42) * mm, "end": v(-6.89, -9.81) * mm});
            skLineSegment(sketch, "E318", {"start": v(-6.89, -9.81) * mm, "end": v(-6.74, -10.1) * mm});
            skLineSegment(sketch, "E319", {"start": v(-6.74, -10.1) * mm, "end": v(-6.5, -10.27) * mm});
            skLineSegment(sketch, "E320", {"start": v(-6.5, -10.27) * mm, "end": v(-6.22, -10.33) * mm});
            skLineSegment(sketch, "E321", {"start": v(-6.22, -10.33) * mm, "end": v(-5.93, -10.25) * mm});
            skLineSegment(sketch, "E322", {"start": v(-5.93, -10.25) * mm, "end": v(-5.74, -10.11) * mm});
            skLineSegment(sketch, "E323", {"start": v(-5.74, -10.11) * mm, "end": v(-5.55, -9.93) * mm});
            skLineSegment(sketch, "E324", {"start": v(-5.55, -9.93) * mm, "end": v(-5.34, -9.7) * mm});
            skLineSegment(sketch, "E325", {"start": v(-5.34, -9.7) * mm, "end": v(-5.08, -9.44) * mm});
            skLineSegment(sketch, "E326", {"start": v(-5.08, -9.44) * mm, "end": v(-4.76, -9.14) * mm});
            skLineSegment(sketch, "E327", {"start": v(-4.76, -9.14) * mm, "end": v(-4.34, -8.8) * mm});
            skLineSegment(sketch, "E328", {"start": v(-4.34, -8.8) * mm, "end": v(-3.81, -8.43) * mm});
            skLineSegment(sketch, "E329", {"start": v(-3.81, -8.43) * mm, "end": v(-3.14, -8.04) * mm});
            skLineSegment(sketch, "E330", {"start": v(-3.14, -8.04) * mm, "end": v(-2.69, -7.8) * mm});
            skLineSegment(sketch, "E331", {"start": v(-2.69, -7.8) * mm, "end": v(-2.23, -7.6) * mm});
            skLineSegment(sketch, "E332", {"start": v(-2.23, -7.6) * mm, "end": v(-1.76, -7.41) * mm});
            skLineSegment(sketch, "E333", {"start": v(-1.76, -7.41) * mm, "end": v(-1.28, -7.26) * mm});
            skLineSegment(sketch, "E334", {"start": v(-1.28, -7.26) * mm, "end": v(-0.79, -7.13) * mm});
            skLineSegment(sketch, "E335", {"start": v(-0.79, -7.13) * mm, "end": v(-0.29, -7.02) * mm});
            skLineSegment(sketch, "E336", {"start": v(-0.29, -7.02) * mm, "end": v(0.22, -6.94) * mm});
            skLineSegment(sketch, "E337", {"start": v(0.22, -6.94) * mm, "end": v(0.74, -6.9) * mm});
            skLineSegment(sketch, "E338", {"start": v(0.74, -6.9) * mm, "end": v(1.12, -6.87) * mm});
            skLineSegment(sketch, "E339", {"start": v(1.12, -6.87) * mm, "end": v(1.42, -6.8) * mm});
            skLineSegment(sketch, "E340", {"start": v(1.42, -6.8) * mm, "end": v(1.51, -6.73) * mm});
            skLineSegment(sketch, "E341", {"start": v(1.51, -6.73) * mm, "end": v(1.56, -6.62) * mm});
            skLineSegment(sketch, "E342", {"start": v(1.56, -6.62) * mm, "end": v(1.54, -6.46) * mm});
            skLineSegment(sketch, "E343", {"start": v(1.54, -6.46) * mm, "end": v(1.45, -6.24) * mm});
            skLineSegment(sketch, "E344", {"start": v(1.45, -6.24) * mm, "end": v(1.26, -6) * mm});
            skLineSegment(sketch, "E345", {"start": v(1.26, -6) * mm, "end": v(1, -5.82) * mm});
            skLineSegment(sketch, "E346", {"start": v(1, -5.82) * mm, "end": v(0.7, -5.69) * mm});
            skLineSegment(sketch, "E347", {"start": v(0.7, -5.69) * mm, "end": v(0.34, -5.6) * mm});
            skLineSegment(sketch, "E348", {"start": v(0.34, -5.6) * mm, "end": v(-0.04, -5.57) * mm});
            skLineSegment(sketch, "E349", {"start": v(-0.04, -5.57) * mm, "end": v(-0.44, -5.57) * mm});
            skLineSegment(sketch, "E350", {"start": v(-0.44, -5.57) * mm, "end": v(-0.84, -5.6) * mm});
            skLineSegment(sketch, "E351", {"start": v(-0.84, -5.6) * mm, "end": v(-1.22, -5.66) * mm});
            skSolve(sketch);
        }
        {
            var Q0;
            Q0 = qSketchRegion(id + "F0", true);
            extrude(context, id + "F1", {"entities" : qUnion([Q0]), "depth" : 6 * mm});
        }
        {
            var Q0;
            Q0=qCreatedBy(makeId("Top.planeOp"),FACE);
            var sketch = newSketch(context, id + "F2", { "sketchPlane" : qUnion([Q0])});
            skLineSegment(sketch, "E352", {"start": v(-27.78, 10.97) * mm, "end": v(-30.48, 9.87) * mm});
            skLineSegment(sketch, "E353", {"start": v(-30.48, 9.87) * mm, "end": v(-33.07, 8.4) * mm});
            skLineSegment(sketch, "E354", {"start": v(-33.07, 8.4) * mm, "end": v(-35.5, 6.61) * mm});
            skLineSegment(sketch, "E355", {"start": v(-35.5, 6.61) * mm, "end": v(-37.74, 4.56) * mm});
            skLineSegment(sketch, "E356", {"start": v(-37.74, 4.56) * mm, "end": v(-39.76, 2.28) * mm});
            skLineSegment(sketch, "E357", {"start": v(-39.76, 2.28) * mm, "end": v(-41.54, -0.18) * mm});
            skLineSegment(sketch, "E358", {"start": v(-41.54, -0.18) * mm, "end": v(-43.03, -2.76) * mm});
            skLineSegment(sketch, "E359", {"start": v(-43.03, -2.76) * mm, "end": v(-44.2, -5.42) * mm});
            skLineSegment(sketch, "E360", {"start": v(-44.2, -5.42) * mm, "end": v(-44.79, -7.15) * mm});
            skLineSegment(sketch, "E361", {"start": v(-44.79, -7.15) * mm, "end": v(-45.26, -8.9) * mm});
            skLineSegment(sketch, "E362", {"start": v(-45.26, -8.9) * mm, "end": v(-45.61, -10.66) * mm});
            skLineSegment(sketch, "E363", {"start": v(-45.61, -10.66) * mm, "end": v(-45.85, -12.43) * mm});
            skLineSegment(sketch, "E364", {"start": v(-45.85, -12.43) * mm, "end": v(-45.98, -14.2) * mm});
            skLineSegment(sketch, "E365", {"start": v(-45.98, -14.2) * mm, "end": v(-46, -16) * mm});
            skLineSegment(sketch, "E366", {"start": v(-46, -16) * mm, "end": v(-45.9, -17.81) * mm});
            skLineSegment(sketch, "E367", {"start": v(-45.9, -17.81) * mm, "end": v(-45.68, -19.63) * mm});
            skLineSegment(sketch, "E368", {"start": v(-45.68, -19.63) * mm, "end": v(-45.59, -20.12) * mm});
            skLineSegment(sketch, "E369", {"start": v(-45.59, -20.12) * mm, "end": v(-45.42, -20.92) * mm});
            skLineSegment(sketch, "E370", {"start": v(-45.42, -20.92) * mm, "end": v(-45.2, -21.92) * mm});
            skLineSegment(sketch, "E371", {"start": v(-45.2, -21.92) * mm, "end": v(-44.93, -23.01) * mm});
            skLineSegment(sketch, "E372", {"start": v(-44.93, -23.01) * mm, "end": v(-44.64, -24.07) * mm});
            skLineSegment(sketch, "E373", {"start": v(-44.64, -24.07) * mm, "end": v(-44.35, -24.98) * mm});
            skLineSegment(sketch, "E374", {"start": v(-44.35, -24.98) * mm, "end": v(-44.07, -25.62) * mm});
            skLineSegment(sketch, "E375", {"start": v(-44.07, -25.62) * mm, "end": v(-43.83, -25.89) * mm});
            skLineSegment(sketch, "E376", {"start": v(-43.83, -25.89) * mm, "end": v(-43.4, -25.87) * mm});
            skLineSegment(sketch, "E377", {"start": v(-43.4, -25.87) * mm, "end": v(-43.17, -25.68) * mm});
            skLineSegment(sketch, "E378", {"start": v(-43.17, -25.68) * mm, "end": v(-43.09, -25.36) * mm});
            skLineSegment(sketch, "E379", {"start": v(-43.09, -25.36) * mm, "end": v(-43.11, -24.96) * mm});
            skLineSegment(sketch, "E380", {"start": v(-43.11, -24.96) * mm, "end": v(-43.34, -24.1) * mm});
            skLineSegment(sketch, "E381", {"start": v(-43.34, -24.1) * mm, "end": v(-43.53, -23.46) * mm});
            skLineSegment(sketch, "E382", {"start": v(-43.53, -23.46) * mm, "end": v(-43.62, -22.99) * mm});
            skLineSegment(sketch, "E383", {"start": v(-43.62, -22.99) * mm, "end": v(-43.7, -22.53) * mm});
            skLineSegment(sketch, "E384", {"start": v(-43.7, -22.53) * mm, "end": v(-43.77, -22.08) * mm});
            skLineSegment(sketch, "E385", {"start": v(-43.77, -22.08) * mm, "end": v(-43.84, -21.64) * mm});
            skLineSegment(sketch, "E386", {"start": v(-43.84, -21.64) * mm, "end": v(-43.9, -21.2) * mm});
            skLineSegment(sketch, "E387", {"start": v(-43.9, -21.2) * mm, "end": v(-43.94, -20.75) * mm});
            skLineSegment(sketch, "E388", {"start": v(-43.94, -20.75) * mm, "end": v(-43.97, -20.29) * mm});
            skLineSegment(sketch, "E389", {"start": v(-43.97, -20.29) * mm, "end": v(-44, -19.8) * mm});
            skLineSegment(sketch, "E390", {"start": v(-44, -19.8) * mm, "end": v(-43.84, -16.57) * mm});
            skLineSegment(sketch, "E391", {"start": v(-43.84, -16.57) * mm, "end": v(-43.18, -13.47) * mm});
            skLineSegment(sketch, "E392", {"start": v(-43.18, -13.47) * mm, "end": v(-42.06, -10.55) * mm});
            skLineSegment(sketch, "E393", {"start": v(-42.06, -10.55) * mm, "end": v(-40.5, -7.87) * mm});
            skLineSegment(sketch, "E394", {"start": v(-40.5, -7.87) * mm, "end": v(-38.54, -5.47) * mm});
            skLineSegment(sketch, "E395", {"start": v(-38.54, -5.47) * mm, "end": v(-36.2, -3.4) * mm});
            skLineSegment(sketch, "E396", {"start": v(-36.2, -3.4) * mm, "end": v(-33.54, -1.7) * mm});
            skLineSegment(sketch, "E397", {"start": v(-33.54, -1.7) * mm, "end": v(-30.56, -0.43) * mm});
            skLineSegment(sketch, "E398", {"start": v(-30.56, -0.43) * mm, "end": v(-28.85, 0.05) * mm});
            skLineSegment(sketch, "E399", {"start": v(-28.85, 0.05) * mm, "end": v(-27.1, 0.37) * mm});
            skLineSegment(sketch, "E400", {"start": v(-27.1, 0.37) * mm, "end": v(-25.34, 0.54) * mm});
            skLineSegment(sketch, "E401", {"start": v(-25.34, 0.54) * mm, "end": v(-23.57, 0.55) * mm});
            skLineSegment(sketch, "E402", {"start": v(-23.57, 0.55) * mm, "end": v(-21.8, 0.4) * mm});
            skLineSegment(sketch, "E403", {"start": v(-21.8, 0.4) * mm, "end": v(-20.06, 0.1) * mm});
            skLineSegment(sketch, "E404", {"start": v(-20.06, 0.1) * mm, "end": v(-18.34, -0.37) * mm});
            skLineSegment(sketch, "E405", {"start": v(-18.34, -0.37) * mm, "end": v(-16.68, -1) * mm});
            skLineSegment(sketch, "E406", {"start": v(-16.68, -1) * mm, "end": v(-15.1, -1.74) * mm});
            skLineSegment(sketch, "E407", {"start": v(-15.1, -1.74) * mm, "end": v(-13.76, -2.5) * mm});
            skLineSegment(sketch, "E408", {"start": v(-13.76, -2.5) * mm, "end": v(-12.63, -3.28) * mm});
            skLineSegment(sketch, "E409", {"start": v(-12.63, -3.28) * mm, "end": v(-11.63, -4.12) * mm});
            skLineSegment(sketch, "E410", {"start": v(-11.63, -4.12) * mm, "end": v(-10.7, -5.03) * mm});
            skLineSegment(sketch, "E411", {"start": v(-10.7, -5.03) * mm, "end": v(-9.79, -6.05) * mm});
            skLineSegment(sketch, "E412", {"start": v(-9.79, -6.05) * mm, "end": v(-8.82, -7.18) * mm});
            skLineSegment(sketch, "E413", {"start": v(-8.82, -7.18) * mm, "end": v(-7.74, -8.46) * mm});
            skLineSegment(sketch, "E414", {"start": v(-7.74, -8.46) * mm, "end": v(-5.28, -7.03) * mm});
            skLineSegment(sketch, "E415", {"start": v(-5.28, -7.03) * mm, "end": v(-5.3, -6.66) * mm});
            skLineSegment(sketch, "E416", {"start": v(-5.3, -6.66) * mm, "end": v(-5.39, -6.21) * mm});
            skLineSegment(sketch, "E417", {"start": v(-5.39, -6.21) * mm, "end": v(-5.49, -5.69) * mm});
            skLineSegment(sketch, "E418", {"start": v(-5.49, -5.69) * mm, "end": v(-5.56, -5.09) * mm});
            skLineSegment(sketch, "E419", {"start": v(-5.56, -5.09) * mm, "end": v(-5.55, -4.41) * mm});
            skLineSegment(sketch, "E420", {"start": v(-5.55, -4.41) * mm, "end": v(-5.44, -3.66) * mm});
            skLineSegment(sketch, "E421", {"start": v(-5.44, -3.66) * mm, "end": v(-5.16, -2.84) * mm});
            skLineSegment(sketch, "E422", {"start": v(-5.16, -2.84) * mm, "end": v(-4.68, -1.96) * mm});
            skLineSegment(sketch, "E423", {"start": v(-4.68, -1.96) * mm, "end": v(-4.52, -1.73) * mm});
            skLineSegment(sketch, "E424", {"start": v(-4.52, -1.73) * mm, "end": v(-4.35, -1.5) * mm});
            skLineSegment(sketch, "E425", {"start": v(-4.35, -1.5) * mm, "end": v(-4.17, -1.29) * mm});
            skLineSegment(sketch, "E426", {"start": v(-4.17, -1.29) * mm, "end": v(-3.98, -1.08) * mm});
            skLineSegment(sketch, "E427", {"start": v(-3.98, -1.08) * mm, "end": v(-3.77, -0.89) * mm});
            skLineSegment(sketch, "E428", {"start": v(-3.77, -0.89) * mm, "end": v(-3.56, -0.7) * mm});
            skLineSegment(sketch, "E429", {"start": v(-3.56, -0.7) * mm, "end": v(-3.34, -0.53) * mm});
            skLineSegment(sketch, "E430", {"start": v(-3.34, -0.53) * mm, "end": v(-3.11, -0.38) * mm});
            skLineSegment(sketch, "E431", {"start": v(-3.11, -0.38) * mm, "end": v(-2.8, -0.2) * mm});
            skLineSegment(sketch, "E432", {"start": v(-2.8, -0.2) * mm, "end": v(-2.49, -0.05) * mm});
            skLineSegment(sketch, "E433", {"start": v(-2.49, -0.05) * mm, "end": v(-2.17, 0.08) * mm});
            skLineSegment(sketch, "E434", {"start": v(-2.17, 0.08) * mm, "end": v(-1.85, 0.19) * mm});
            skLineSegment(sketch, "E435", {"start": v(-1.85, 0.19) * mm, "end": v(-1.56, 0.28) * mm});
            skLineSegment(sketch, "E436", {"start": v(-1.56, 0.28) * mm, "end": v(-1.3, 0.37) * mm});
            skLineSegment(sketch, "E437", {"start": v(-1.3, 0.37) * mm, "end": v(-1.07, 0.46) * mm});
            skLineSegment(sketch, "E438", {"start": v(-1.07, 0.46) * mm, "end": v(-0.9, 0.55) * mm});
            skLineSegment(sketch, "E439", {"start": v(-0.9, 0.55) * mm, "end": v(-0.9, 3.45) * mm});
            skLineSegment(sketch, "E440", {"start": v(-0.9, 3.45) * mm, "end": v(-4.56, 4) * mm});
            skLineSegment(sketch, "E441", {"start": v(-4.56, 4) * mm, "end": v(-7.99, 5.18) * mm});
            skLineSegment(sketch, "E442", {"start": v(-7.99, 5.18) * mm, "end": v(-11.11, 6.92) * mm});
            skLineSegment(sketch, "E443", {"start": v(-11.11, 6.92) * mm, "end": v(-13.86, 9.15) * mm});
            skLineSegment(sketch, "E444", {"start": v(-13.86, 9.15) * mm, "end": v(-16.16, 11.83) * mm});
            skLineSegment(sketch, "E445", {"start": v(-16.16, 11.83) * mm, "end": v(-17.93, 14.9) * mm});
            skLineSegment(sketch, "E446", {"start": v(-17.93, 14.9) * mm, "end": v(-19.11, 18.32) * mm});
            skLineSegment(sketch, "E447", {"start": v(-19.11, 18.32) * mm, "end": v(-19.63, 22.02) * mm});
            skLineSegment(sketch, "E448", {"start": v(-19.63, 22.02) * mm, "end": v(-19.56, 24.81) * mm});
            skLineSegment(sketch, "E449", {"start": v(-19.56, 24.81) * mm, "end": v(-19.14, 27.51) * mm});
            skLineSegment(sketch, "E450", {"start": v(-19.14, 27.51) * mm, "end": v(-18.37, 30.08) * mm});
            skLineSegment(sketch, "E451", {"start": v(-18.37, 30.08) * mm, "end": v(-17.27, 32.5) * mm});
            skLineSegment(sketch, "E452", {"start": v(-17.27, 32.5) * mm, "end": v(-15.84, 34.74) * mm});
            skLineSegment(sketch, "E453", {"start": v(-15.84, 34.74) * mm, "end": v(-14.11, 36.78) * mm});
            skLineSegment(sketch, "E454", {"start": v(-14.11, 36.78) * mm, "end": v(-12.09, 38.6) * mm});
            skLineSegment(sketch, "E455", {"start": v(-12.09, 38.6) * mm, "end": v(-9.78, 40.15) * mm});
            skLineSegment(sketch, "E456", {"start": v(-9.78, 40.15) * mm, "end": v(-9.4, 40.37) * mm});
            skLineSegment(sketch, "E457", {"start": v(-9.4, 40.37) * mm, "end": v(-9.01, 40.57) * mm});
            skLineSegment(sketch, "E458", {"start": v(-9.01, 40.57) * mm, "end": v(-8.61, 40.77) * mm});
            skLineSegment(sketch, "E459", {"start": v(-8.61, 40.77) * mm, "end": v(-8.21, 40.96) * mm});
            skLineSegment(sketch, "E460", {"start": v(-8.21, 40.96) * mm, "end": v(-7.8, 41.14) * mm});
            skLineSegment(sketch, "E461", {"start": v(-7.8, 41.14) * mm, "end": v(-7.4, 41.31) * mm});
            skLineSegment(sketch, "E462", {"start": v(-7.4, 41.31) * mm, "end": v(-6.98, 41.47) * mm});
            skLineSegment(sketch, "E463", {"start": v(-6.98, 41.47) * mm, "end": v(-6.57, 41.62) * mm});
            skLineSegment(sketch, "E464", {"start": v(-6.57, 41.62) * mm, "end": v(-6.01, 41.78) * mm});
            skLineSegment(sketch, "E465", {"start": v(-6.01, 41.78) * mm, "end": v(-5.48, 41.9) * mm});
            skLineSegment(sketch, "E466", {"start": v(-5.48, 41.9) * mm, "end": v(-4.99, 42) * mm});
            skLineSegment(sketch, "E467", {"start": v(-4.99, 42) * mm, "end": v(-4.55, 42.14) * mm});
            skLineSegment(sketch, "E468", {"start": v(-4.55, 42.14) * mm, "end": v(-4.19, 42.31) * mm});
            skLineSegment(sketch, "E469", {"start": v(-4.19, 42.31) * mm, "end": v(-3.92, 42.57) * mm});
            skLineSegment(sketch, "E470", {"start": v(-3.92, 42.57) * mm, "end": v(-3.76, 42.95) * mm});
            skLineSegment(sketch, "E471", {"start": v(-3.76, 42.95) * mm, "end": v(-3.73, 43.47) * mm});
            skLineSegment(sketch, "E472", {"start": v(-3.73, 43.47) * mm, "end": v(-6.34, 43.05) * mm});
            skLineSegment(sketch, "E473", {"start": v(-6.34, 43.05) * mm, "end": v(-8.92, 42.33) * mm});
            skLineSegment(sketch, "E474", {"start": v(-8.92, 42.33) * mm, "end": v(-11.43, 41.33) * mm});
            skLineSegment(sketch, "E475", {"start": v(-11.43, 41.33) * mm, "end": v(-13.86, 40.08) * mm});
            skLineSegment(sketch, "E476", {"start": v(-13.86, 40.08) * mm, "end": v(-16.15, 38.6) * mm});
            skLineSegment(sketch, "E477", {"start": v(-16.15, 38.6) * mm, "end": v(-18.3, 36.94) * mm});
            skLineSegment(sketch, "E478", {"start": v(-18.3, 36.94) * mm, "end": v(-20.26, 35.1) * mm});
            skLineSegment(sketch, "E479", {"start": v(-20.26, 35.1) * mm, "end": v(-22, 33.13) * mm});
            skLineSegment(sketch, "E480", {"start": v(-22, 33.13) * mm, "end": v(-23.81, 30.63) * mm});
            skLineSegment(sketch, "E481", {"start": v(-23.81, 30.63) * mm, "end": v(-25.28, 28.06) * mm});
            skLineSegment(sketch, "E482", {"start": v(-25.28, 28.06) * mm, "end": v(-26.42, 25.4) * mm});
            skLineSegment(sketch, "E483", {"start": v(-26.42, 25.4) * mm, "end": v(-27.25, 22.68) * mm});
            skLineSegment(sketch, "E484", {"start": v(-27.25, 22.68) * mm, "end": v(-27.78, 19.88) * mm});
            skLineSegment(sketch, "E485", {"start": v(-27.78, 19.88) * mm, "end": v(-28.04, 17) * mm});
            skLineSegment(sketch, "E486", {"start": v(-28.04, 17) * mm, "end": v(-28.03, 14.03) * mm});
            skLineSegment(sketch, "E487", {"start": v(-28.03, 14.03) * mm, "end": v(-27.78, 10.97) * mm});
            skLineSegment(sketch, "E488", {"start": v(0.9, 3.45) * mm, "end": v(0.9, 0.55) * mm});
            skLineSegment(sketch, "E489", {"start": v(0.9, 0.55) * mm, "end": v(1.19, 0.41) * mm});
            skLineSegment(sketch, "E490", {"start": v(1.19, 0.41) * mm, "end": v(1.57, 0.28) * mm});
            skLineSegment(sketch, "E491", {"start": v(1.57, 0.28) * mm, "end": v(2.02, 0.13) * mm});
            skLineSegment(sketch, "E492", {"start": v(2.02, 0.13) * mm, "end": v(2.53, -0.07) * mm});
            skLineSegment(sketch, "E493", {"start": v(2.53, -0.07) * mm, "end": v(3.07, -0.35) * mm});
            skLineSegment(sketch, "E494", {"start": v(3.07, -0.35) * mm, "end": v(3.62, -0.74) * mm});
            skLineSegment(sketch, "E495", {"start": v(3.62, -0.74) * mm, "end": v(4.17, -1.26) * mm});
            skLineSegment(sketch, "E496", {"start": v(4.17, -1.26) * mm, "end": v(4.68, -1.95) * mm});
            skLineSegment(sketch, "E497", {"start": v(4.68, -1.95) * mm, "end": v(5.17, -2.85) * mm});
            skLineSegment(sketch, "E498", {"start": v(5.17, -2.85) * mm, "end": v(5.44, -3.67) * mm});
            skLineSegment(sketch, "E499", {"start": v(5.44, -3.67) * mm, "end": v(5.56, -4.42) * mm});
            skLineSegment(sketch, "E500", {"start": v(5.56, -4.42) * mm, "end": v(5.56, -5.1) * mm});
            skLineSegment(sketch, "E501", {"start": v(5.56, -5.1) * mm, "end": v(5.5, -5.69) * mm});
            skLineSegment(sketch, "E502", {"start": v(5.5, -5.69) * mm, "end": v(5.4, -6.2) * mm});
            skLineSegment(sketch, "E503", {"start": v(5.4, -6.2) * mm, "end": v(5.31, -6.65) * mm});
            skLineSegment(sketch, "E504", {"start": v(5.31, -6.65) * mm, "end": v(5.29, -7.02) * mm});
            skLineSegment(sketch, "E505", {"start": v(5.29, -7.02) * mm, "end": v(7.75, -8.44) * mm});
            skLineSegment(sketch, "E506", {"start": v(7.75, -8.44) * mm, "end": v(8.83, -7.17) * mm});
            skLineSegment(sketch, "E507", {"start": v(8.83, -7.17) * mm, "end": v(9.8, -6.04) * mm});
            skLineSegment(sketch, "E508", {"start": v(9.8, -6.04) * mm, "end": v(10.7, -5.03) * mm});
            skLineSegment(sketch, "E509", {"start": v(10.7, -5.03) * mm, "end": v(11.64, -4.11) * mm});
            skLineSegment(sketch, "E510", {"start": v(11.64, -4.11) * mm, "end": v(12.64, -3.27) * mm});
            skLineSegment(sketch, "E511", {"start": v(12.64, -3.27) * mm, "end": v(13.77, -2.49) * mm});
            skLineSegment(sketch, "E512", {"start": v(13.77, -2.49) * mm, "end": v(15.1, -1.73) * mm});
            skLineSegment(sketch, "E513", {"start": v(15.1, -1.73) * mm, "end": v(16.68, -1) * mm});
            skLineSegment(sketch, "E514", {"start": v(16.68, -1) * mm, "end": v(18.35, -0.37) * mm});
            skLineSegment(sketch, "E515", {"start": v(18.35, -0.37) * mm, "end": v(20.07, 0.1) * mm});
            skLineSegment(sketch, "E516", {"start": v(20.07, 0.1) * mm, "end": v(21.81, 0.4) * mm});
            skLineSegment(sketch, "E517", {"start": v(21.81, 0.4) * mm, "end": v(23.57, 0.55) * mm});
            skLineSegment(sketch, "E518", {"start": v(23.57, 0.55) * mm, "end": v(25.34, 0.54) * mm});
            skLineSegment(sketch, "E519", {"start": v(25.34, 0.54) * mm, "end": v(27.1, 0.37) * mm});
            skLineSegment(sketch, "E520", {"start": v(27.1, 0.37) * mm, "end": v(28.85, 0.05) * mm});
            skLineSegment(sketch, "E521", {"start": v(28.85, 0.05) * mm, "end": v(30.56, -0.43) * mm});
            skLineSegment(sketch, "E522", {"start": v(30.56, -0.43) * mm, "end": v(33.54, -1.7) * mm});
            skLineSegment(sketch, "E523", {"start": v(33.54, -1.7) * mm, "end": v(36.22, -3.4) * mm});
            skLineSegment(sketch, "E524", {"start": v(36.22, -3.4) * mm, "end": v(38.55, -5.47) * mm});
            skLineSegment(sketch, "E525", {"start": v(38.55, -5.47) * mm, "end": v(40.5, -7.87) * mm});
            skLineSegment(sketch, "E526", {"start": v(40.5, -7.87) * mm, "end": v(42.06, -10.55) * mm});
            skLineSegment(sketch, "E527", {"start": v(42.06, -10.55) * mm, "end": v(43.18, -13.47) * mm});
            skLineSegment(sketch, "E528", {"start": v(43.18, -13.47) * mm, "end": v(43.84, -16.57) * mm});
            skLineSegment(sketch, "E529", {"start": v(43.84, -16.57) * mm, "end": v(44, -19.8) * mm});
            skLineSegment(sketch, "E530", {"start": v(44, -19.8) * mm, "end": v(43.98, -20.28) * mm});
            skLineSegment(sketch, "E531", {"start": v(43.98, -20.28) * mm, "end": v(43.95, -20.74) * mm});
            skLineSegment(sketch, "E532", {"start": v(43.95, -20.74) * mm, "end": v(43.9, -21.18) * mm});
            skLineSegment(sketch, "E533", {"start": v(43.9, -21.18) * mm, "end": v(43.85, -21.62) * mm});
            skLineSegment(sketch, "E534", {"start": v(43.85, -21.62) * mm, "end": v(43.78, -22.05) * mm});
            skLineSegment(sketch, "E535", {"start": v(43.78, -22.05) * mm, "end": v(43.7, -22.5) * mm});
            skLineSegment(sketch, "E536", {"start": v(43.7, -22.5) * mm, "end": v(43.63, -22.94) * mm});
            skLineSegment(sketch, "E537", {"start": v(43.63, -22.94) * mm, "end": v(43.54, -23.4) * mm});
            skLineSegment(sketch, "E538", {"start": v(43.54, -23.4) * mm, "end": v(43.35, -24.05) * mm});
            skLineSegment(sketch, "E539", {"start": v(43.35, -24.05) * mm, "end": v(43.12, -24.94) * mm});
            skLineSegment(sketch, "E540", {"start": v(43.12, -24.94) * mm, "end": v(43.1, -25.35) * mm});
            skLineSegment(sketch, "E541", {"start": v(43.1, -25.35) * mm, "end": v(43.18, -25.68) * mm});
            skLineSegment(sketch, "E542", {"start": v(43.18, -25.68) * mm, "end": v(43.41, -25.87) * mm});
            skLineSegment(sketch, "E543", {"start": v(43.41, -25.87) * mm, "end": v(43.84, -25.89) * mm});
            skLineSegment(sketch, "E544", {"start": v(43.84, -25.89) * mm, "end": v(44.08, -25.62) * mm});
            skLineSegment(sketch, "E545", {"start": v(44.08, -25.62) * mm, "end": v(44.35, -24.98) * mm});
            skLineSegment(sketch, "E546", {"start": v(44.35, -24.98) * mm, "end": v(44.64, -24.07) * mm});
            skLineSegment(sketch, "E547", {"start": v(44.64, -24.07) * mm, "end": v(44.93, -23.01) * mm});
            skLineSegment(sketch, "E548", {"start": v(44.93, -23.01) * mm, "end": v(45.2, -21.92) * mm});
            skLineSegment(sketch, "E549", {"start": v(45.2, -21.92) * mm, "end": v(45.43, -20.92) * mm});
            skLineSegment(sketch, "E550", {"start": v(45.43, -20.92) * mm, "end": v(45.6, -20.12) * mm});
            skLineSegment(sketch, "E551", {"start": v(45.6, -20.12) * mm, "end": v(45.68, -19.63) * mm});
            skLineSegment(sketch, "E552", {"start": v(45.68, -19.63) * mm, "end": v(45.9, -17.81) * mm});
            skLineSegment(sketch, "E553", {"start": v(45.9, -17.81) * mm, "end": v(46, -16) * mm});
            skLineSegment(sketch, "E554", {"start": v(46, -16) * mm, "end": v(45.98, -14.2) * mm});
            skLineSegment(sketch, "E555", {"start": v(45.98, -14.2) * mm, "end": v(45.86, -12.43) * mm});
            skLineSegment(sketch, "E556", {"start": v(45.86, -12.43) * mm, "end": v(45.62, -10.66) * mm});
            skLineSegment(sketch, "E557", {"start": v(45.62, -10.66) * mm, "end": v(45.26, -8.9) * mm});
            skLineSegment(sketch, "E558", {"start": v(45.26, -8.9) * mm, "end": v(44.8, -7.15) * mm});
            skLineSegment(sketch, "E559", {"start": v(44.8, -7.15) * mm, "end": v(44.2, -5.42) * mm});
            skLineSegment(sketch, "E560", {"start": v(44.2, -5.42) * mm, "end": v(43.03, -2.76) * mm});
            skLineSegment(sketch, "E561", {"start": v(43.03, -2.76) * mm, "end": v(41.54, -0.17) * mm});
            skLineSegment(sketch, "E562", {"start": v(41.54, -0.17) * mm, "end": v(39.77, 2.28) * mm});
            skLineSegment(sketch, "E563", {"start": v(39.77, 2.28) * mm, "end": v(37.74, 4.56) * mm});
            skLineSegment(sketch, "E564", {"start": v(37.74, 4.56) * mm, "end": v(35.5, 6.61) * mm});
            skLineSegment(sketch, "E565", {"start": v(35.5, 6.61) * mm, "end": v(33.07, 8.4) * mm});
            skLineSegment(sketch, "E566", {"start": v(33.07, 8.4) * mm, "end": v(30.5, 9.87) * mm});
            skLineSegment(sketch, "E567", {"start": v(30.5, 9.87) * mm, "end": v(27.78, 10.97) * mm});
            skLineSegment(sketch, "E568", {"start": v(27.78, 10.97) * mm, "end": v(28.03, 14) * mm});
            skLineSegment(sketch, "E569", {"start": v(28.03, 14) * mm, "end": v(28.04, 16.97) * mm});
            skLineSegment(sketch, "E570", {"start": v(28.04, 16.97) * mm, "end": v(27.78, 19.85) * mm});
            skLineSegment(sketch, "E571", {"start": v(27.78, 19.85) * mm, "end": v(27.25, 22.66) * mm});
            skLineSegment(sketch, "E572", {"start": v(27.25, 22.66) * mm, "end": v(26.43, 25.39) * mm});
            skLineSegment(sketch, "E573", {"start": v(26.43, 25.39) * mm, "end": v(25.3, 28.04) * mm});
            skLineSegment(sketch, "E574", {"start": v(25.3, 28.04) * mm, "end": v(23.84, 30.61) * mm});
            skLineSegment(sketch, "E575", {"start": v(23.84, 30.61) * mm, "end": v(22.04, 33.1) * mm});
            skLineSegment(sketch, "E576", {"start": v(22.04, 33.1) * mm, "end": v(20.28, 35.08) * mm});
            skLineSegment(sketch, "E577", {"start": v(20.28, 35.08) * mm, "end": v(18.32, 36.92) * mm});
            skLineSegment(sketch, "E578", {"start": v(18.32, 36.92) * mm, "end": v(16.2, 38.59) * mm});
            skLineSegment(sketch, "E579", {"start": v(16.2, 38.59) * mm, "end": v(13.9, 40.06) * mm});
            skLineSegment(sketch, "E580", {"start": v(13.9, 40.06) * mm, "end": v(11.5, 41.3) * mm});
            skLineSegment(sketch, "E581", {"start": v(11.5, 41.3) * mm, "end": v(9, 42.3) * mm});
            skLineSegment(sketch, "E582", {"start": v(9, 42.3) * mm, "end": v(6.42, 43.03) * mm});
            skLineSegment(sketch, "E583", {"start": v(6.42, 43.03) * mm, "end": v(3.8, 43.46) * mm});
            skLineSegment(sketch, "E584", {"start": v(3.8, 43.46) * mm, "end": v(3.68, 43.01) * mm});
            skLineSegment(sketch, "E585", {"start": v(3.68, 43.01) * mm, "end": v(3.8, 42.66) * mm});
            skLineSegment(sketch, "E586", {"start": v(3.8, 42.66) * mm, "end": v(4.09, 42.4) * mm});
            skLineSegment(sketch, "E587", {"start": v(4.09, 42.4) * mm, "end": v(4.51, 42.18) * mm});
            skLineSegment(sketch, "E588", {"start": v(4.51, 42.18) * mm, "end": v(5.01, 42.02) * mm});
            skLineSegment(sketch, "E589", {"start": v(5.01, 42.02) * mm, "end": v(5.54, 41.9) * mm});
            skLineSegment(sketch, "E590", {"start": v(5.54, 41.9) * mm, "end": v(6.05, 41.77) * mm});
            skLineSegment(sketch, "E591", {"start": v(6.05, 41.77) * mm, "end": v(6.48, 41.65) * mm});
            skLineSegment(sketch, "E592", {"start": v(6.48, 41.65) * mm, "end": v(7.68, 41.2) * mm});
            skLineSegment(sketch, "E593", {"start": v(7.68, 41.2) * mm, "end": v(8.84, 40.67) * mm});
            skLineSegment(sketch, "E594", {"start": v(8.84, 40.67) * mm, "end": v(9.96, 40.05) * mm});
            skLineSegment(sketch, "E595", {"start": v(9.96, 40.05) * mm, "end": v(11.04, 39.36) * mm});
            skLineSegment(sketch, "E596", {"start": v(11.04, 39.36) * mm, "end": v(12.08, 38.6) * mm});
            skLineSegment(sketch, "E597", {"start": v(12.08, 38.6) * mm, "end": v(13.06, 37.78) * mm});
            skLineSegment(sketch, "E598", {"start": v(13.06, 37.78) * mm, "end": v(14, 36.9) * mm});
            skLineSegment(sketch, "E599", {"start": v(14, 36.9) * mm, "end": v(14.86, 35.97) * mm});
            skLineSegment(sketch, "E600", {"start": v(14.86, 35.97) * mm, "end": v(16.05, 34.47) * mm});
            skLineSegment(sketch, "E601", {"start": v(16.05, 34.47) * mm, "end": v(17.07, 32.88) * mm});
            skLineSegment(sketch, "E602", {"start": v(17.07, 32.88) * mm, "end": v(17.92, 31.22) * mm});
            skLineSegment(sketch, "E603", {"start": v(17.92, 31.22) * mm, "end": v(18.6, 29.5) * mm});
            skLineSegment(sketch, "E604", {"start": v(18.6, 29.5) * mm, "end": v(19.1, 27.7) * mm});
            skLineSegment(sketch, "E605", {"start": v(19.1, 27.7) * mm, "end": v(19.45, 25.87) * mm});
            skLineSegment(sketch, "E606", {"start": v(19.45, 25.87) * mm, "end": v(19.62, 23.99) * mm});
            skLineSegment(sketch, "E607", {"start": v(19.62, 23.99) * mm, "end": v(19.63, 22.08) * mm});
            skLineSegment(sketch, "E608", {"start": v(19.63, 22.08) * mm, "end": v(19.13, 18.37) * mm});
            skLineSegment(sketch, "E609", {"start": v(19.13, 18.37) * mm, "end": v(17.95, 14.94) * mm});
            skLineSegment(sketch, "E610", {"start": v(17.95, 14.94) * mm, "end": v(16.18, 11.86) * mm});
            skLineSegment(sketch, "E611", {"start": v(16.18, 11.86) * mm, "end": v(13.89, 9.17) * mm});
            skLineSegment(sketch, "E612", {"start": v(13.89, 9.17) * mm, "end": v(11.14, 6.93) * mm});
            skLineSegment(sketch, "E613", {"start": v(11.14, 6.93) * mm, "end": v(8, 5.2) * mm});
            skLineSegment(sketch, "E614", {"start": v(8, 5.2) * mm, "end": v(4.57, 4.01) * mm});
            skLineSegment(sketch, "E615", {"start": v(4.57, 4.01) * mm, "end": v(0.9, 3.45) * mm});
            skLineSegment(sketch, "E616", {"start": v(-6.87, -10.06) * mm, "end": v(-4.87, -17.23) * mm});
            skLineSegment(sketch, "E617", {"start": v(-4.87, -17.23) * mm, "end": v(-5.31, -23.85) * mm});
            skLineSegment(sketch, "E618", {"start": v(-5.31, -23.85) * mm, "end": v(-7.78, -29.62) * mm});
            skLineSegment(sketch, "E619", {"start": v(-7.78, -29.62) * mm, "end": v(-11.85, -34.24) * mm});
            skLineSegment(sketch, "E620", {"start": v(-11.85, -34.24) * mm, "end": v(-17.1, -37.4) * mm});
            skLineSegment(sketch, "E621", {"start": v(-17.1, -37.4) * mm, "end": v(-23.11, -38.82) * mm});
            skLineSegment(sketch, "E622", {"start": v(-23.11, -38.82) * mm, "end": v(-29.46, -38.16) * mm});
            skLineSegment(sketch, "E623", {"start": v(-29.46, -38.16) * mm, "end": v(-35.72, -35.15) * mm});
            skLineSegment(sketch, "E624", {"start": v(-35.72, -35.15) * mm, "end": v(-36.3, -34.7) * mm});
            skLineSegment(sketch, "E625", {"start": v(-36.3, -34.7) * mm, "end": v(-36.86, -34.26) * mm});
            skLineSegment(sketch, "E626", {"start": v(-36.86, -34.26) * mm, "end": v(-37.4, -33.79) * mm});
            skLineSegment(sketch, "E627", {"start": v(-37.4, -33.79) * mm, "end": v(-37.94, -33.3) * mm});
            skLineSegment(sketch, "E628", {"start": v(-37.94, -33.3) * mm, "end": v(-38.2, -33.04) * mm});
            skLineSegment(sketch, "E629", {"start": v(-38.2, -33.04) * mm, "end": v(-38.46, -32.74) * mm});
            skLineSegment(sketch, "E630", {"start": v(-38.46, -32.74) * mm, "end": v(-38.71, -32.46) * mm});
            skLineSegment(sketch, "E631", {"start": v(-38.71, -32.46) * mm, "end": v(-38.95, -32.24) * mm});
            skLineSegment(sketch, "E632", {"start": v(-38.95, -32.24) * mm, "end": v(-39.08, -32.17) * mm});
            skLineSegment(sketch, "E633", {"start": v(-39.08, -32.17) * mm, "end": v(-39.24, -32.13) * mm});
            skLineSegment(sketch, "E634", {"start": v(-39.24, -32.13) * mm, "end": v(-39.4, -32.12) * mm});
            skLineSegment(sketch, "E635", {"start": v(-39.4, -32.12) * mm, "end": v(-39.55, -32.15) * mm});
            skLineSegment(sketch, "E636", {"start": v(-39.55, -32.15) * mm, "end": v(-39.68, -32.2) * mm});
            skLineSegment(sketch, "E637", {"start": v(-39.68, -32.2) * mm, "end": v(-39.79, -32.3) * mm});
            skLineSegment(sketch, "E638", {"start": v(-39.79, -32.3) * mm, "end": v(-39.84, -32.44) * mm});
            skLineSegment(sketch, "E639", {"start": v(-39.84, -32.44) * mm, "end": v(-39.84, -32.62) * mm});
            skLineSegment(sketch, "E640", {"start": v(-39.84, -32.62) * mm, "end": v(-39.66, -33.07) * mm});
            skLineSegment(sketch, "E641", {"start": v(-39.66, -33.07) * mm, "end": v(-39.3, -33.61) * mm});
            skLineSegment(sketch, "E642", {"start": v(-39.3, -33.61) * mm, "end": v(-38.8, -34.2) * mm});
            skLineSegment(sketch, "E643", {"start": v(-38.8, -34.2) * mm, "end": v(-38.22, -34.82) * mm});
            skLineSegment(sketch, "E644", {"start": v(-38.22, -34.82) * mm, "end": v(-37.61, -35.41) * mm});
            skLineSegment(sketch, "E645", {"start": v(-37.61, -35.41) * mm, "end": v(-37.02, -35.97) * mm});
            skLineSegment(sketch, "E646", {"start": v(-37.02, -35.97) * mm, "end": v(-36.49, -36.44) * mm});
            skLineSegment(sketch, "E647", {"start": v(-36.49, -36.44) * mm, "end": v(-36.08, -36.8) * mm});
            skLineSegment(sketch, "E648", {"start": v(-36.08, -36.8) * mm, "end": v(-32.69, -39.28) * mm});
            skLineSegment(sketch, "E649", {"start": v(-32.69, -39.28) * mm, "end": v(-29, -41.2) * mm});
            skLineSegment(sketch, "E650", {"start": v(-29, -41.2) * mm, "end": v(-25.1, -42.54) * mm});
            skLineSegment(sketch, "E651", {"start": v(-25.1, -42.54) * mm, "end": v(-21.07, -43.3) * mm});
            skLineSegment(sketch, "E652", {"start": v(-21.07, -43.3) * mm, "end": v(-16.96, -43.47) * mm});
            skLineSegment(sketch, "E653", {"start": v(-16.96, -43.47) * mm, "end": v(-12.86, -43.04) * mm});
            skLineSegment(sketch, "E654", {"start": v(-12.86, -43.04) * mm, "end": v(-8.85, -42.02) * mm});
            skLineSegment(sketch, "E655", {"start": v(-8.85, -42.02) * mm, "end": v(-4.98, -40.38) * mm});
            skLineSegment(sketch, "E656", {"start": v(-4.98, -40.38) * mm, "end": v(-4.57, -40.14) * mm});
            skLineSegment(sketch, "E657", {"start": v(-4.57, -40.14) * mm, "end": v(-3.93, -39.74) * mm});
            skLineSegment(sketch, "E658", {"start": v(-3.93, -39.74) * mm, "end": v(-3.14, -39.25) * mm});
            skLineSegment(sketch, "E659", {"start": v(-3.14, -39.25) * mm, "end": v(-2.3, -38.7) * mm});
            skLineSegment(sketch, "E660", {"start": v(-2.3, -38.7) * mm, "end": v(-1.49, -38.2) * mm});
            skLineSegment(sketch, "E661", {"start": v(-1.49, -38.2) * mm, "end": v(-0.78, -37.75) * mm});
            skLineSegment(sketch, "E662", {"start": v(-0.78, -37.75) * mm, "end": v(-0.26, -37.44) * mm});
            skLineSegment(sketch, "E663", {"start": v(-0.26, -37.44) * mm, "end": v(-0.01, -37.33) * mm});
            skLineSegment(sketch, "E664", {"start": v(-0.01, -37.33) * mm, "end": v(0.26, -37.44) * mm});
            skLineSegment(sketch, "E665", {"start": v(0.26, -37.44) * mm, "end": v(0.78, -37.74) * mm});
            skLineSegment(sketch, "E666", {"start": v(0.78, -37.74) * mm, "end": v(1.48, -38.17) * mm});
            skLineSegment(sketch, "E667", {"start": v(1.48, -38.17) * mm, "end": v(2.28, -38.68) * mm});
            skLineSegment(sketch, "E668", {"start": v(2.28, -38.68) * mm, "end": v(3.1, -39.2) * mm});
            skLineSegment(sketch, "E669", {"start": v(3.1, -39.2) * mm, "end": v(3.86, -39.7) * mm});
            skLineSegment(sketch, "E670", {"start": v(3.86, -39.7) * mm, "end": v(4.5, -40.1) * mm});
            skLineSegment(sketch, "E671", {"start": v(4.5, -40.1) * mm, "end": v(4.9, -40.34) * mm});
            skLineSegment(sketch, "E672", {"start": v(4.9, -40.34) * mm, "end": v(8.76, -41.99) * mm});
            skLineSegment(sketch, "E673", {"start": v(8.76, -41.99) * mm, "end": v(12.77, -43.03) * mm});
            skLineSegment(sketch, "E674", {"start": v(12.77, -43.03) * mm, "end": v(16.87, -43.47) * mm});
            skLineSegment(sketch, "E675", {"start": v(16.87, -43.47) * mm, "end": v(20.99, -43.3) * mm});
            skLineSegment(sketch, "E676", {"start": v(20.99, -43.3) * mm, "end": v(25.03, -42.56) * mm});
            skLineSegment(sketch, "E677", {"start": v(25.03, -42.56) * mm, "end": v(28.94, -41.23) * mm});
            skLineSegment(sketch, "E678", {"start": v(28.94, -41.23) * mm, "end": v(32.63, -39.32) * mm});
            skLineSegment(sketch, "E679", {"start": v(32.63, -39.32) * mm, "end": v(36.02, -36.85) * mm});
            skLineSegment(sketch, "E680", {"start": v(36.02, -36.85) * mm, "end": v(36.42, -36.5) * mm});
            skLineSegment(sketch, "E681", {"start": v(36.42, -36.5) * mm, "end": v(36.95, -36.03) * mm});
            skLineSegment(sketch, "E682", {"start": v(36.95, -36.03) * mm, "end": v(37.55, -35.47) * mm});
            skLineSegment(sketch, "E683", {"start": v(37.55, -35.47) * mm, "end": v(38.17, -34.87) * mm});
            skLineSegment(sketch, "E684", {"start": v(38.17, -34.87) * mm, "end": v(38.76, -34.25) * mm});
            skLineSegment(sketch, "E685", {"start": v(38.76, -34.25) * mm, "end": v(39.27, -33.66) * mm});
            skLineSegment(sketch, "E686", {"start": v(39.27, -33.66) * mm, "end": v(39.64, -33.13) * mm});
            skLineSegment(sketch, "E687", {"start": v(39.64, -33.13) * mm, "end": v(39.83, -32.69) * mm});
            skLineSegment(sketch, "E688", {"start": v(39.83, -32.69) * mm, "end": v(39.85, -32.5) * mm});
            skLineSegment(sketch, "E689", {"start": v(39.85, -32.5) * mm, "end": v(39.8, -32.34) * mm});
            skLineSegment(sketch, "E690", {"start": v(39.8, -32.34) * mm, "end": v(39.71, -32.23) * mm});
            skLineSegment(sketch, "E691", {"start": v(39.71, -32.23) * mm, "end": v(39.6, -32.15) * mm});
            skLineSegment(sketch, "E692", {"start": v(39.6, -32.15) * mm, "end": v(39.45, -32.12) * mm});
            skLineSegment(sketch, "E693", {"start": v(39.45, -32.12) * mm, "end": v(39.3, -32.11) * mm});
            skLineSegment(sketch, "E694", {"start": v(39.3, -32.11) * mm, "end": v(39.15, -32.14) * mm});
            skLineSegment(sketch, "E695", {"start": v(39.15, -32.14) * mm, "end": v(39.02, -32.2) * mm});
            skLineSegment(sketch, "E696", {"start": v(39.02, -32.2) * mm, "end": v(38.91, -32.28) * mm});
            skLineSegment(sketch, "E697", {"start": v(38.91, -32.28) * mm, "end": v(38.79, -32.4) * mm});
            skLineSegment(sketch, "E698", {"start": v(38.79, -32.4) * mm, "end": v(38.66, -32.53) * mm});
            skLineSegment(sketch, "E699", {"start": v(38.66, -32.53) * mm, "end": v(38.52, -32.68) * mm});
            skLineSegment(sketch, "E700", {"start": v(38.52, -32.68) * mm, "end": v(38.25, -33) * mm});
            skLineSegment(sketch, "E701", {"start": v(38.25, -33) * mm, "end": v(38.01, -33.24) * mm});
            skLineSegment(sketch, "E702", {"start": v(38.01, -33.24) * mm, "end": v(37.46, -33.74) * mm});
            skLineSegment(sketch, "E703", {"start": v(37.46, -33.74) * mm, "end": v(36.92, -34.22) * mm});
            skLineSegment(sketch, "E704", {"start": v(36.92, -34.22) * mm, "end": v(36.36, -34.67) * mm});
            skLineSegment(sketch, "E705", {"start": v(36.36, -34.67) * mm, "end": v(35.76, -35.12) * mm});
            skLineSegment(sketch, "E706", {"start": v(35.76, -35.12) * mm, "end": v(29.45, -38.15) * mm});
            skLineSegment(sketch, "E707", {"start": v(29.45, -38.15) * mm, "end": v(23.08, -38.8) * mm});
            skLineSegment(sketch, "E708", {"start": v(23.08, -38.8) * mm, "end": v(17.05, -37.38) * mm});
            skLineSegment(sketch, "E709", {"start": v(17.05, -37.38) * mm, "end": v(11.8, -34.2) * mm});
            skLineSegment(sketch, "E710", {"start": v(11.8, -34.2) * mm, "end": v(7.74, -29.56) * mm});
            skLineSegment(sketch, "E711", {"start": v(7.74, -29.56) * mm, "end": v(5.29, -23.78) * mm});
            skLineSegment(sketch, "E712", {"start": v(5.29, -23.78) * mm, "end": v(4.86, -17.18) * mm});
            skLineSegment(sketch, "E713", {"start": v(4.86, -17.18) * mm, "end": v(6.88, -10.06) * mm});
            skLineSegment(sketch, "E714", {"start": v(6.88, -10.06) * mm, "end": v(4.38, -8.62) * mm});
            skLineSegment(sketch, "E715", {"start": v(4.38, -8.62) * mm, "end": v(4.15, -8.76) * mm});
            skLineSegment(sketch, "E716", {"start": v(4.15, -8.76) * mm, "end": v(3.92, -8.95) * mm});
            skLineSegment(sketch, "E717", {"start": v(3.92, -8.95) * mm, "end": v(3.67, -9.17) * mm});
            skLineSegment(sketch, "E718", {"start": v(3.67, -9.17) * mm, "end": v(3.4, -9.4) * mm});
            skLineSegment(sketch, "E719", {"start": v(3.4, -9.4) * mm, "end": v(3.09, -9.66) * mm});
            skLineSegment(sketch, "E720", {"start": v(3.09, -9.66) * mm, "end": v(2.74, -9.9) * mm});
            skLineSegment(sketch, "E721", {"start": v(2.74, -9.9) * mm, "end": v(2.34, -10.12) * mm});
            skLineSegment(sketch, "E722", {"start": v(2.34, -10.12) * mm, "end": v(1.88, -10.3) * mm});
            skLineSegment(sketch, "E723", {"start": v(1.88, -10.3) * mm, "end": v(1.43, -10.44) * mm});
            skLineSegment(sketch, "E724", {"start": v(1.43, -10.44) * mm, "end": v(0.99, -10.54) * mm});
            skLineSegment(sketch, "E725", {"start": v(0.99, -10.54) * mm, "end": v(0.54, -10.6) * mm});
            skLineSegment(sketch, "E726", {"start": v(0.54, -10.6) * mm, "end": v(0.1, -10.63) * mm});
            skLineSegment(sketch, "E727", {"start": v(0.1, -10.63) * mm, "end": v(-0.34, -10.62) * mm});
            skLineSegment(sketch, "E728", {"start": v(-0.34, -10.62) * mm, "end": v(-0.79, -10.57) * mm});
            skLineSegment(sketch, "E729", {"start": v(-0.79, -10.57) * mm, "end": v(-1.24, -10.49) * mm});
            skLineSegment(sketch, "E730", {"start": v(-1.24, -10.49) * mm, "end": v(-1.69, -10.36) * mm});
            skLineSegment(sketch, "E731", {"start": v(-1.69, -10.36) * mm, "end": v(-2.8, -9.92) * mm});
            skLineSegment(sketch, "E732", {"start": v(-2.8, -9.92) * mm, "end": v(-3.46, -9.48) * mm});
            skLineSegment(sketch, "E733", {"start": v(-3.46, -9.48) * mm, "end": v(-3.82, -9.1) * mm});
            skLineSegment(sketch, "E734", {"start": v(-3.82, -9.1) * mm, "end": v(-4.05, -8.85) * mm});
            skLineSegment(sketch, "E735", {"start": v(-4.05, -8.85) * mm, "end": v(-4.3, -8.76) * mm});
            skLineSegment(sketch, "E736", {"start": v(-4.3, -8.76) * mm, "end": v(-4.75, -8.9) * mm});
            skLineSegment(sketch, "E737", {"start": v(-4.75, -8.9) * mm, "end": v(-5.55, -9.32) * mm});
            skLineSegment(sketch, "E738", {"start": v(-5.55, -9.32) * mm, "end": v(-6.87, -10.06) * mm});
            skLineSegment(sketch, "E739", {"start": v(-9.28, -28.56) * mm, "end": v(-8.97, -28.19) * mm});
            skLineSegment(sketch, "E740", {"start": v(-8.97, -28.19) * mm, "end": v(-8.6, -27.53) * mm});
            skLineSegment(sketch, "E741", {"start": v(-8.6, -27.53) * mm, "end": v(-8.2, -26.66) * mm});
            skLineSegment(sketch, "E742", {"start": v(-8.2, -26.66) * mm, "end": v(-7.8, -25.7) * mm});
            skLineSegment(sketch, "E743", {"start": v(-7.8, -25.7) * mm, "end": v(-7.44, -24.7) * mm});
            skLineSegment(sketch, "E744", {"start": v(-7.44, -24.7) * mm, "end": v(-7.15, -23.78) * mm});
            skLineSegment(sketch, "E745", {"start": v(-7.15, -23.78) * mm, "end": v(-6.95, -23.02) * mm});
            skLineSegment(sketch, "E746", {"start": v(-6.95, -23.02) * mm, "end": v(-6.87, -22.52) * mm});
            skLineSegment(sketch, "E747", {"start": v(-6.87, -22.52) * mm, "end": v(-7.3, -22.25) * mm});
            skLineSegment(sketch, "E748", {"start": v(-7.3, -22.25) * mm, "end": v(-7.75, -22.01) * mm});
            skLineSegment(sketch, "E749", {"start": v(-7.75, -22.01) * mm, "end": v(-8.25, -21.78) * mm});
            skLineSegment(sketch, "E750", {"start": v(-8.25, -21.78) * mm, "end": v(-8.82, -21.5) * mm});
            skLineSegment(sketch, "E751", {"start": v(-8.82, -21.5) * mm, "end": v(-9.46, -21.17) * mm});
            skLineSegment(sketch, "E752", {"start": v(-9.46, -21.17) * mm, "end": v(-10.18, -20.75) * mm});
            skLineSegment(sketch, "E753", {"start": v(-10.18, -20.75) * mm, "end": v(-11, -20.2) * mm});
            skLineSegment(sketch, "E754", {"start": v(-11, -20.2) * mm, "end": v(-11.91, -19.48) * mm});
            skLineSegment(sketch, "E755", {"start": v(-11.91, -19.48) * mm, "end": v(-12.47, -19) * mm});
            skLineSegment(sketch, "E756", {"start": v(-12.47, -19) * mm, "end": v(-13, -18.52) * mm});
            skLineSegment(sketch, "E757", {"start": v(-13, -18.52) * mm, "end": v(-13.5, -18.01) * mm});
            skLineSegment(sketch, "E758", {"start": v(-13.5, -18.01) * mm, "end": v(-13.98, -17.49) * mm});
            skLineSegment(sketch, "E759", {"start": v(-13.98, -17.49) * mm, "end": v(-14.45, -16.95) * mm});
            skLineSegment(sketch, "E760", {"start": v(-14.45, -16.95) * mm, "end": v(-14.89, -16.39) * mm});
            skLineSegment(sketch, "E761", {"start": v(-14.89, -16.39) * mm, "end": v(-15.31, -15.8) * mm});
            skLineSegment(sketch, "E762", {"start": v(-15.31, -15.8) * mm, "end": v(-15.72, -15.2) * mm});
            skLineSegment(sketch, "E763", {"start": v(-15.72, -15.2) * mm, "end": v(-16.67, -13.59) * mm});
            skLineSegment(sketch, "E764", {"start": v(-16.67, -13.59) * mm, "end": v(-17.4, -12.03) * mm});
            skLineSegment(sketch, "E765", {"start": v(-17.4, -12.03) * mm, "end": v(-17.94, -10.5) * mm});
            skLineSegment(sketch, "E766", {"start": v(-17.94, -10.5) * mm, "end": v(-18.31, -8.97) * mm});
            skLineSegment(sketch, "E767", {"start": v(-18.31, -8.97) * mm, "end": v(-18.53, -7.41) * mm});
            skLineSegment(sketch, "E768", {"start": v(-18.53, -7.41) * mm, "end": v(-18.62, -5.79) * mm});
            skLineSegment(sketch, "E769", {"start": v(-18.62, -5.79) * mm, "end": v(-18.61, -4.07) * mm});
            skLineSegment(sketch, "E770", {"start": v(-18.61, -4.07) * mm, "end": v(-18.53, -2.23) * mm});
            skLineSegment(sketch, "E771", {"start": v(-18.53, -2.23) * mm, "end": v(-19.25, -2.02) * mm});
            skLineSegment(sketch, "E772", {"start": v(-19.25, -2.02) * mm, "end": v(-19.93, -1.84) * mm});
            skLineSegment(sketch, "E773", {"start": v(-19.93, -1.84) * mm, "end": v(-20.57, -1.7) * mm});
            skLineSegment(sketch, "E774", {"start": v(-20.57, -1.7) * mm, "end": v(-21.2, -1.58) * mm});
            skLineSegment(sketch, "E775", {"start": v(-21.2, -1.58) * mm, "end": v(-21.83, -1.49) * mm});
            skLineSegment(sketch, "E776", {"start": v(-21.83, -1.49) * mm, "end": v(-22.48, -1.4) * mm});
            skLineSegment(sketch, "E777", {"start": v(-22.48, -1.4) * mm, "end": v(-23.17, -1.33) * mm});
            skLineSegment(sketch, "E778", {"start": v(-23.17, -1.33) * mm, "end": v(-23.92, -1.26) * mm});
            skLineSegment(sketch, "E779", {"start": v(-23.92, -1.26) * mm, "end": v(-24.43, -1.24) * mm});
            skLineSegment(sketch, "E780", {"start": v(-24.43, -1.24) * mm, "end": v(-24.78, -1.28) * mm});
            skLineSegment(sketch, "E781", {"start": v(-24.78, -1.28) * mm, "end": v(-25, -1.4) * mm});
            skLineSegment(sketch, "E782", {"start": v(-25, -1.4) * mm, "end": v(-25.14, -1.58) * mm});
            skLineSegment(sketch, "E783", {"start": v(-25.14, -1.58) * mm, "end": v(-25.2, -1.84) * mm});
            skLineSegment(sketch, "E784", {"start": v(-25.2, -1.84) * mm, "end": v(-25.22, -2.18) * mm});
            skLineSegment(sketch, "E785", {"start": v(-25.22, -2.18) * mm, "end": v(-25.23, -2.6) * mm});
            skLineSegment(sketch, "E786", {"start": v(-25.23, -2.6) * mm, "end": v(-25.26, -3.09) * mm});
            skLineSegment(sketch, "E787", {"start": v(-25.26, -3.09) * mm, "end": v(-25.34, -4.76) * mm});
            skLineSegment(sketch, "E788", {"start": v(-25.34, -4.76) * mm, "end": v(-25.3, -6.47) * mm});
            skLineSegment(sketch, "E789", {"start": v(-25.3, -6.47) * mm, "end": v(-25.14, -8.2) * mm});
            skLineSegment(sketch, "E790", {"start": v(-25.14, -8.2) * mm, "end": v(-24.85, -9.92) * mm});
            skLineSegment(sketch, "E791", {"start": v(-24.85, -9.92) * mm, "end": v(-24.46, -11.62) * mm});
            skLineSegment(sketch, "E792", {"start": v(-24.46, -11.62) * mm, "end": v(-23.95, -13.28) * mm});
            skLineSegment(sketch, "E793", {"start": v(-23.95, -13.28) * mm, "end": v(-23.35, -14.88) * mm});
            skLineSegment(sketch, "E794", {"start": v(-23.35, -14.88) * mm, "end": v(-22.64, -16.4) * mm});
            skLineSegment(sketch, "E795", {"start": v(-22.64, -16.4) * mm, "end": v(-22.07, -17.46) * mm});
            skLineSegment(sketch, "E796", {"start": v(-22.07, -17.46) * mm, "end": v(-21.48, -18.46) * mm});
            skLineSegment(sketch, "E797", {"start": v(-21.48, -18.46) * mm, "end": v(-20.86, -19.4) * mm});
            skLineSegment(sketch, "E798", {"start": v(-20.86, -19.4) * mm, "end": v(-20.21, -20.3) * mm});
            skLineSegment(sketch, "E799", {"start": v(-20.21, -20.3) * mm, "end": v(-19.52, -21.16) * mm});
            skLineSegment(sketch, "E800", {"start": v(-19.52, -21.16) * mm, "end": v(-18.78, -22) * mm});
            skLineSegment(sketch, "E801", {"start": v(-18.78, -22) * mm, "end": v(-17.99, -22.85) * mm});
            skLineSegment(sketch, "E802", {"start": v(-17.99, -22.85) * mm, "end": v(-17.12, -23.7) * mm});
            skLineSegment(sketch, "E803", {"start": v(-17.12, -23.7) * mm, "end": v(-16.4, -24.34) * mm});
            skLineSegment(sketch, "E804", {"start": v(-16.4, -24.34) * mm, "end": v(-15.5, -25.05) * mm});
            skLineSegment(sketch, "E805", {"start": v(-15.5, -25.05) * mm, "end": v(-14.5, -25.8) * mm});
            skLineSegment(sketch, "E806", {"start": v(-14.5, -25.8) * mm, "end": v(-13.4, -26.53) * mm});
            skLineSegment(sketch, "E807", {"start": v(-13.4, -26.53) * mm, "end": v(-12.28, -27.21) * mm});
            skLineSegment(sketch, "E808", {"start": v(-12.28, -27.21) * mm, "end": v(-11.2, -27.8) * mm});
            skLineSegment(sketch, "E809", {"start": v(-11.2, -27.8) * mm, "end": v(-10.17, -28.27) * mm});
            skLineSegment(sketch, "E810", {"start": v(-10.17, -28.27) * mm, "end": v(-9.28, -28.56) * mm});
            skLineSegment(sketch, "E811", {"start": v(-1.63, 20.25) * mm, "end": v(-3.38, 20.06) * mm});
            skLineSegment(sketch, "E812", {"start": v(-3.38, 20.06) * mm, "end": v(-5.08, 19.77) * mm});
            skLineSegment(sketch, "E813", {"start": v(-5.08, 19.77) * mm, "end": v(-6.74, 19.38) * mm});
            skLineSegment(sketch, "E814", {"start": v(-6.74, 19.38) * mm, "end": v(-8.36, 18.89) * mm});
            skLineSegment(sketch, "E815", {"start": v(-8.36, 18.89) * mm, "end": v(-9.93, 18.28) * mm});
            skLineSegment(sketch, "E816", {"start": v(-9.93, 18.28) * mm, "end": v(-11.47, 17.57) * mm});
            skLineSegment(sketch, "E817", {"start": v(-11.47, 17.57) * mm, "end": v(-12.98, 16.73) * mm});
            skLineSegment(sketch, "E818", {"start": v(-12.98, 16.73) * mm, "end": v(-14.46, 15.78) * mm});
            skLineSegment(sketch, "E819", {"start": v(-14.46, 15.78) * mm, "end": v(-14.92, 15.47) * mm});
            skLineSegment(sketch, "E820", {"start": v(-14.92, 15.47) * mm, "end": v(-15.28, 15.24) * mm});
            skLineSegment(sketch, "E821", {"start": v(-15.28, 15.24) * mm, "end": v(-15.53, 15.03) * mm});
            skLineSegment(sketch, "E822", {"start": v(-15.53, 15.03) * mm, "end": v(-15.64, 14.8) * mm});
            skLineSegment(sketch, "E823", {"start": v(-15.64, 14.8) * mm, "end": v(-15.6, 14.48) * mm});
            skLineSegment(sketch, "E824", {"start": v(-15.6, 14.48) * mm, "end": v(-15.4, 14.05) * mm});
            skLineSegment(sketch, "E825", {"start": v(-15.4, 14.05) * mm, "end": v(-15, 13.44) * mm});
            skLineSegment(sketch, "E826", {"start": v(-15, 13.44) * mm, "end": v(-14.43, 12.6) * mm});
            skLineSegment(sketch, "E827", {"start": v(-14.43, 12.6) * mm, "end": v(-14.23, 12.35) * mm});
            skLineSegment(sketch, "E828", {"start": v(-14.23, 12.35) * mm, "end": v(-13.9, 11.95) * mm});
            skLineSegment(sketch, "E829", {"start": v(-13.9, 11.95) * mm, "end": v(-13.51, 11.48) * mm});
            skLineSegment(sketch, "E830", {"start": v(-13.51, 11.48) * mm, "end": v(-13.07, 10.98) * mm});
            skLineSegment(sketch, "E831", {"start": v(-13.07, 10.98) * mm, "end": v(-12.63, 10.5) * mm});
            skLineSegment(sketch, "E832", {"start": v(-12.63, 10.5) * mm, "end": v(-12.22, 10.1) * mm});
            skLineSegment(sketch, "E833", {"start": v(-12.22, 10.1) * mm, "end": v(-11.89, 9.8) * mm});
            skLineSegment(sketch, "E834", {"start": v(-11.89, 9.8) * mm, "end": v(-11.67, 9.7) * mm});
            skLineSegment(sketch, "E835", {"start": v(-11.67, 9.7) * mm, "end": v(-11.51, 9.78) * mm});
            skLineSegment(sketch, "E836", {"start": v(-11.51, 9.78) * mm, "end": v(-11.14, 10) * mm});
            skLineSegment(sketch, "E837", {"start": v(-11.14, 10) * mm, "end": v(-10.63, 10.32) * mm});
            skLineSegment(sketch, "E838", {"start": v(-10.63, 10.32) * mm, "end": v(-10.03, 10.68) * mm});
            skLineSegment(sketch, "E839", {"start": v(-10.03, 10.68) * mm, "end": v(-9.42, 11.06) * mm});
            skLineSegment(sketch, "E840", {"start": v(-9.42, 11.06) * mm, "end": v(-8.85, 11.41) * mm});
            skLineSegment(sketch, "E841", {"start": v(-8.85, 11.41) * mm, "end": v(-8.4, 11.68) * mm});
            skLineSegment(sketch, "E842", {"start": v(-8.4, 11.68) * mm, "end": v(-8.11, 11.84) * mm});
            skLineSegment(sketch, "E843", {"start": v(-8.11, 11.84) * mm, "end": v(-7, 12.33) * mm});
            skLineSegment(sketch, "E844", {"start": v(-7, 12.33) * mm, "end": v(-5.83, 12.75) * mm});
            skLineSegment(sketch, "E845", {"start": v(-5.83, 12.75) * mm, "end": v(-4.62, 13.1) * mm});
            skLineSegment(sketch, "E846", {"start": v(-4.62, 13.1) * mm, "end": v(-3.38, 13.38) * mm});
            skLineSegment(sketch, "E847", {"start": v(-3.38, 13.38) * mm, "end": v(-2.13, 13.58) * mm});
            skLineSegment(sketch, "E848", {"start": v(-2.13, 13.58) * mm, "end": v(-0.88, 13.69) * mm});
            skLineSegment(sketch, "E849", {"start": v(-0.88, 13.69) * mm, "end": v(0.36, 13.7) * mm});
            skLineSegment(sketch, "E850", {"start": v(0.36, 13.7) * mm, "end": v(1.58, 13.62) * mm});
            skLineSegment(sketch, "E851", {"start": v(1.58, 13.62) * mm, "end": v(2.76, 13.47) * mm});
            skLineSegment(sketch, "E852", {"start": v(2.76, 13.47) * mm, "end": v(3.9, 13.26) * mm});
            skLineSegment(sketch, "E853", {"start": v(3.9, 13.26) * mm, "end": v(5, 13) * mm});
            skLineSegment(sketch, "E854", {"start": v(5, 13) * mm, "end": v(6.06, 12.68) * mm});
            skLineSegment(sketch, "E855", {"start": v(6.06, 12.68) * mm, "end": v(7.1, 12.3) * mm});
            skLineSegment(sketch, "E856", {"start": v(7.1, 12.3) * mm, "end": v(8.13, 11.84) * mm});
            skLineSegment(sketch, "E857", {"start": v(8.13, 11.84) * mm, "end": v(9.15, 11.3) * mm});
            skLineSegment(sketch, "E858", {"start": v(9.15, 11.3) * mm, "end": v(10.17, 10.69) * mm});
            skLineSegment(sketch, "E859", {"start": v(10.17, 10.69) * mm, "end": v(10.75, 10.3) * mm});
            skLineSegment(sketch, "E860", {"start": v(10.75, 10.3) * mm, "end": v(11.17, 10) * mm});
            skLineSegment(sketch, "E861", {"start": v(11.17, 10) * mm, "end": v(11.5, 9.82) * mm});
            skLineSegment(sketch, "E862", {"start": v(11.5, 9.82) * mm, "end": v(11.77, 9.76) * mm});
            skLineSegment(sketch, "E863", {"start": v(11.77, 9.76) * mm, "end": v(12.04, 9.86) * mm});
            skLineSegment(sketch, "E864", {"start": v(12.04, 9.86) * mm, "end": v(12.35, 10.12) * mm});
            skLineSegment(sketch, "E865", {"start": v(12.35, 10.12) * mm, "end": v(12.75, 10.57) * mm});
            skLineSegment(sketch, "E866", {"start": v(12.75, 10.57) * mm, "end": v(13.3, 11.22) * mm});
            skLineSegment(sketch, "E867", {"start": v(13.3, 11.22) * mm, "end": v(13.54, 11.52) * mm});
            skLineSegment(sketch, "E868", {"start": v(13.54, 11.52) * mm, "end": v(13.87, 11.92) * mm});
            skLineSegment(sketch, "E869", {"start": v(13.87, 11.92) * mm, "end": v(14.23, 12.39) * mm});
            skLineSegment(sketch, "E870", {"start": v(14.23, 12.39) * mm, "end": v(14.61, 12.9) * mm});
            skLineSegment(sketch, "E871", {"start": v(14.61, 12.9) * mm, "end": v(14.98, 13.4) * mm});
            skLineSegment(sketch, "E872", {"start": v(14.98, 13.4) * mm, "end": v(15.3, 13.87) * mm});
            skLineSegment(sketch, "E873", {"start": v(15.3, 13.87) * mm, "end": v(15.55, 14.29) * mm});
            skLineSegment(sketch, "E874", {"start": v(15.55, 14.29) * mm, "end": v(15.7, 14.62) * mm});
            skLineSegment(sketch, "E875", {"start": v(15.7, 14.62) * mm, "end": v(15.52, 15.04) * mm});
            skLineSegment(sketch, "E876", {"start": v(15.52, 15.04) * mm, "end": v(14.84, 15.6) * mm});
            skLineSegment(sketch, "E877", {"start": v(14.84, 15.6) * mm, "end": v(13.81, 16.25) * mm});
            skLineSegment(sketch, "E878", {"start": v(13.81, 16.25) * mm, "end": v(12.58, 16.93) * mm});
            skLineSegment(sketch, "E879", {"start": v(12.58, 16.93) * mm, "end": v(11.29, 17.58) * mm});
            skLineSegment(sketch, "E880", {"start": v(11.29, 17.58) * mm, "end": v(10.08, 18.15) * mm});
            skLineSegment(sketch, "E881", {"start": v(10.08, 18.15) * mm, "end": v(9.1, 18.59) * mm});
            skLineSegment(sketch, "E882", {"start": v(9.1, 18.59) * mm, "end": v(8.51, 18.83) * mm});
            skLineSegment(sketch, "E883", {"start": v(8.51, 18.83) * mm, "end": v(7.3, 19.22) * mm});
            skLineSegment(sketch, "E884", {"start": v(7.3, 19.22) * mm, "end": v(6.07, 19.56) * mm});
            skLineSegment(sketch, "E885", {"start": v(6.07, 19.56) * mm, "end": v(4.8, 19.84) * mm});
            skLineSegment(sketch, "E886", {"start": v(4.8, 19.84) * mm, "end": v(3.51, 20.06) * mm});
            skLineSegment(sketch, "E887", {"start": v(3.51, 20.06) * mm, "end": v(2.22, 20.21) * mm});
            skLineSegment(sketch, "E888", {"start": v(2.22, 20.21) * mm, "end": v(0.92, 20.3) * mm});
            skLineSegment(sketch, "E889", {"start": v(0.92, 20.3) * mm, "end": v(-0.36, 20.3) * mm});
            skLineSegment(sketch, "E890", {"start": v(-0.36, 20.3) * mm, "end": v(-1.63, 20.25) * mm});
            skLineSegment(sketch, "E891", {"start": v(18.53, -2.23) * mm, "end": v(18.61, -3.64) * mm});
            skLineSegment(sketch, "E892", {"start": v(18.61, -3.64) * mm, "end": v(18.66, -4.92) * mm});
            skLineSegment(sketch, "E893", {"start": v(18.66, -4.92) * mm, "end": v(18.66, -6.1) * mm});
            skLineSegment(sketch, "E894", {"start": v(18.66, -6.1) * mm, "end": v(18.59, -7.25) * mm});
            skLineSegment(sketch, "E895", {"start": v(18.59, -7.25) * mm, "end": v(18.44, -8.38) * mm});
            skLineSegment(sketch, "E896", {"start": v(18.44, -8.38) * mm, "end": v(18.19, -9.54) * mm});
            skLineSegment(sketch, "E897", {"start": v(18.19, -9.54) * mm, "end": v(17.83, -10.78) * mm});
            skLineSegment(sketch, "E898", {"start": v(17.83, -10.78) * mm, "end": v(17.33, -12.13) * mm});
            skLineSegment(sketch, "E899", {"start": v(17.33, -12.13) * mm, "end": v(16.69, -13.56) * mm});
            skLineSegment(sketch, "E900", {"start": v(16.69, -13.56) * mm, "end": v(15.92, -14.92) * mm});
            skLineSegment(sketch, "E901", {"start": v(15.92, -14.92) * mm, "end": v(15.04, -16.2) * mm});
            skLineSegment(sketch, "E902", {"start": v(15.04, -16.2) * mm, "end": v(14.06, -17.4) * mm});
            skLineSegment(sketch, "E903", {"start": v(14.06, -17.4) * mm, "end": v(12.98, -18.53) * mm});
            skLineSegment(sketch, "E904", {"start": v(12.98, -18.53) * mm, "end": v(11.81, -19.55) * mm});
            skLineSegment(sketch, "E905", {"start": v(11.81, -19.55) * mm, "end": v(10.57, -20.48) * mm});
            skLineSegment(sketch, "E906", {"start": v(10.57, -20.48) * mm, "end": v(9.25, -21.31) * mm});
            skLineSegment(sketch, "E907", {"start": v(9.25, -21.31) * mm, "end": v(8.4, -21.77) * mm});
            skLineSegment(sketch, "E908", {"start": v(8.4, -21.77) * mm, "end": v(7.76, -22.07) * mm});
            skLineSegment(sketch, "E909", {"start": v(7.76, -22.07) * mm, "end": v(7.31, -22.28) * mm});
            skLineSegment(sketch, "E910", {"start": v(7.31, -22.28) * mm, "end": v(7.04, -22.47) * mm});
            skLineSegment(sketch, "E911", {"start": v(7.04, -22.47) * mm, "end": v(6.92, -22.7) * mm});
            skLineSegment(sketch, "E912", {"start": v(6.92, -22.7) * mm, "end": v(6.94, -23.02) * mm});
            skLineSegment(sketch, "E913", {"start": v(6.94, -23.02) * mm, "end": v(7.07, -23.52) * mm});
            skLineSegment(sketch, "E914", {"start": v(7.07, -23.52) * mm, "end": v(7.3, -24.25) * mm});
            skLineSegment(sketch, "E915", {"start": v(7.3, -24.25) * mm, "end": v(7.44, -24.7) * mm});
            skLineSegment(sketch, "E916", {"start": v(7.44, -24.7) * mm, "end": v(7.62, -25.21) * mm});
            skLineSegment(sketch, "E917", {"start": v(7.62, -25.21) * mm, "end": v(7.83, -25.76) * mm});
            skLineSegment(sketch, "E918", {"start": v(7.83, -25.76) * mm, "end": v(8.06, -26.32) * mm});
            skLineSegment(sketch, "E919", {"start": v(8.06, -26.32) * mm, "end": v(8.3, -26.88) * mm});
            skLineSegment(sketch, "E920", {"start": v(8.3, -26.88) * mm, "end": v(8.55, -27.4) * mm});
            skLineSegment(sketch, "E921", {"start": v(8.55, -27.4) * mm, "end": v(8.8, -27.87) * mm});
            skLineSegment(sketch, "E922", {"start": v(8.8, -27.87) * mm, "end": v(9.04, -28.27) * mm});
            skLineSegment(sketch, "E923", {"start": v(9.04, -28.27) * mm, "end": v(9.32, -28.44) * mm});
            skLineSegment(sketch, "E924", {"start": v(9.32, -28.44) * mm, "end": v(9.75, -28.43) * mm});
            skLineSegment(sketch, "E925", {"start": v(9.75, -28.43) * mm, "end": v(10.28, -28.27) * mm});
            skLineSegment(sketch, "E926", {"start": v(10.28, -28.27) * mm, "end": v(10.86, -28.02) * mm});
            skLineSegment(sketch, "E927", {"start": v(10.86, -28.02) * mm, "end": v(11.44, -27.7) * mm});
            skLineSegment(sketch, "E928", {"start": v(11.44, -27.7) * mm, "end": v(11.99, -27.39) * mm});
            skLineSegment(sketch, "E929", {"start": v(11.99, -27.39) * mm, "end": v(12.44, -27.11) * mm});
            skLineSegment(sketch, "E930", {"start": v(12.44, -27.11) * mm, "end": v(12.76, -26.92) * mm});
            skLineSegment(sketch, "E931", {"start": v(12.76, -26.92) * mm, "end": v(14.5, -25.81) * mm});
            skLineSegment(sketch, "E932", {"start": v(14.5, -25.81) * mm, "end": v(16.14, -24.56) * mm});
            skLineSegment(sketch, "E933", {"start": v(16.14, -24.56) * mm, "end": v(17.7, -23.16) * mm});
            skLineSegment(sketch, "E934", {"start": v(17.7, -23.16) * mm, "end": v(19.13, -21.65) * mm});
            skLineSegment(sketch, "E935", {"start": v(19.13, -21.65) * mm, "end": v(20.43, -20.02) * mm});
            skLineSegment(sketch, "E936", {"start": v(20.43, -20.02) * mm, "end": v(21.6, -18.3) * mm});
            skLineSegment(sketch, "E937", {"start": v(21.6, -18.3) * mm, "end": v(22.61, -16.5) * mm});
            skLineSegment(sketch, "E938", {"start": v(22.61, -16.5) * mm, "end": v(23.46, -14.61) * mm});
            skLineSegment(sketch, "E939", {"start": v(23.46, -14.61) * mm, "end": v(23.9, -13.42) * mm});
            skLineSegment(sketch, "E940", {"start": v(23.9, -13.42) * mm, "end": v(24.29, -12.24) * mm});
            skLineSegment(sketch, "E941", {"start": v(24.29, -12.24) * mm, "end": v(24.6, -11.07) * mm});
            skLineSegment(sketch, "E942", {"start": v(24.6, -11.07) * mm, "end": v(24.87, -9.9) * mm});
            skLineSegment(sketch, "E943", {"start": v(24.87, -9.9) * mm, "end": v(25.07, -8.72) * mm});
            skLineSegment(sketch, "E944", {"start": v(25.07, -8.72) * mm, "end": v(25.2, -7.52) * mm});
            skLineSegment(sketch, "E945", {"start": v(25.2, -7.52) * mm, "end": v(25.3, -6.28) * mm});
            skLineSegment(sketch, "E946", {"start": v(25.3, -6.28) * mm, "end": v(25.32, -5) * mm});
            skLineSegment(sketch, "E947", {"start": v(25.32, -5) * mm, "end": v(25.3, -4.3) * mm});
            skLineSegment(sketch, "E948", {"start": v(25.3, -4.3) * mm, "end": v(25.27, -3.63) * mm});
            skLineSegment(sketch, "E949", {"start": v(25.27, -3.63) * mm, "end": v(25.23, -2.96) * mm});
            skLineSegment(sketch, "E950", {"start": v(25.23, -2.96) * mm, "end": v(25.2, -2.28) * mm});
            skLineSegment(sketch, "E951", {"start": v(25.2, -2.28) * mm, "end": v(25.16, -1.83) * mm});
            skLineSegment(sketch, "E952", {"start": v(25.16, -1.83) * mm, "end": v(25.06, -1.52) * mm});
            skLineSegment(sketch, "E953", {"start": v(25.06, -1.52) * mm, "end": v(24.9, -1.32) * mm});
            skLineSegment(sketch, "E954", {"start": v(24.9, -1.32) * mm, "end": v(24.7, -1.22) * mm});
            skLineSegment(sketch, "E955", {"start": v(24.7, -1.22) * mm, "end": v(24.44, -1.2) * mm});
            skLineSegment(sketch, "E956", {"start": v(24.44, -1.2) * mm, "end": v(24.13, -1.21) * mm});
            skLineSegment(sketch, "E957", {"start": v(24.13, -1.21) * mm, "end": v(23.77, -1.25) * mm});
            skLineSegment(sketch, "E958", {"start": v(23.77, -1.25) * mm, "end": v(23.36, -1.3) * mm});
            skLineSegment(sketch, "E959", {"start": v(23.36, -1.3) * mm, "end": v(22.7, -1.35) * mm});
            skLineSegment(sketch, "E960", {"start": v(22.7, -1.35) * mm, "end": v(22.08, -1.42) * mm});
            skLineSegment(sketch, "E961", {"start": v(22.08, -1.42) * mm, "end": v(21.49, -1.5) * mm});
            skLineSegment(sketch, "E962", {"start": v(21.49, -1.5) * mm, "end": v(20.92, -1.61) * mm});
            skLineSegment(sketch, "E963", {"start": v(20.92, -1.61) * mm, "end": v(20.35, -1.73) * mm});
            skLineSegment(sketch, "E964", {"start": v(20.35, -1.73) * mm, "end": v(19.77, -1.87) * mm});
            skLineSegment(sketch, "E965", {"start": v(19.77, -1.87) * mm, "end": v(19.17, -2.04) * mm});
            skLineSegment(sketch, "E966", {"start": v(19.17, -2.04) * mm, "end": v(18.53, -2.23) * mm});
            skSolve(sketch);
        }
        {
            var Q0;
            Q0=makeQuery(id+"F2.imprint","IMPRINT",FACE,{"disambiguationData":[TD([[makeQuery(id+"F2.imprint","IMPRINT",EDGE,{"derivedFrom":sQuery(id+"F2.wireOp",EDGE,"E488")}),1.0]])]});
            var Q1;
            Q1=makeQuery(id+"F2.imprint","IMPRINT",FACE,{"disambiguationData":[TD([[makeQuery(id+"F2.imprint","IMPRINT",EDGE,{"derivedFrom":sQuery(id+"F2.wireOp",EDGE,"E616")}),1.0]])]});
            var Q2;
            Q2=makeQuery(id+"F2.imprint","IMPRINT",FACE,{"disambiguationData":[TD([[makeQuery(id+"F2.imprint","IMPRINT",EDGE,{"derivedFrom":sQuery(id+"F2.wireOp",EDGE,"E352")}),1.0]])]});
            var Q3;
            Q3=makeQuery(id+"F2.imprint","IMPRINT",FACE,{"disambiguationData":[TD([[makeQuery(id+"F2.imprint","IMPRINT",EDGE,{"derivedFrom":sQuery(id+"F2.wireOp",EDGE,"E739")}),1.0]])]});
            var Q4;
            Q4=makeQuery(id+"F2.imprint","IMPRINT",FACE,{"disambiguationData":[TD([[makeQuery(id+"F2.imprint","IMPRINT",EDGE,{"derivedFrom":sQuery(id+"F2.wireOp",EDGE,"E891")}),1.0]])]});
            var Q5;
            Q5=makeQuery(id+"F2.imprint","IMPRINT",FACE,{"disambiguationData":[TD([[makeQuery(id+"F2.imprint","IMPRINT",EDGE,{"derivedFrom":sQuery(id+"F2.wireOp",EDGE,"E811")}),1.0]])]});
            extrude(context, id + "F3", {"entities" : qUnion([Q0, Q1, Q2, Q3, Q4, Q5]), "operationType" : NewBodyOperationType.ADD, "depth" : 3 * mm});
        }
    });
